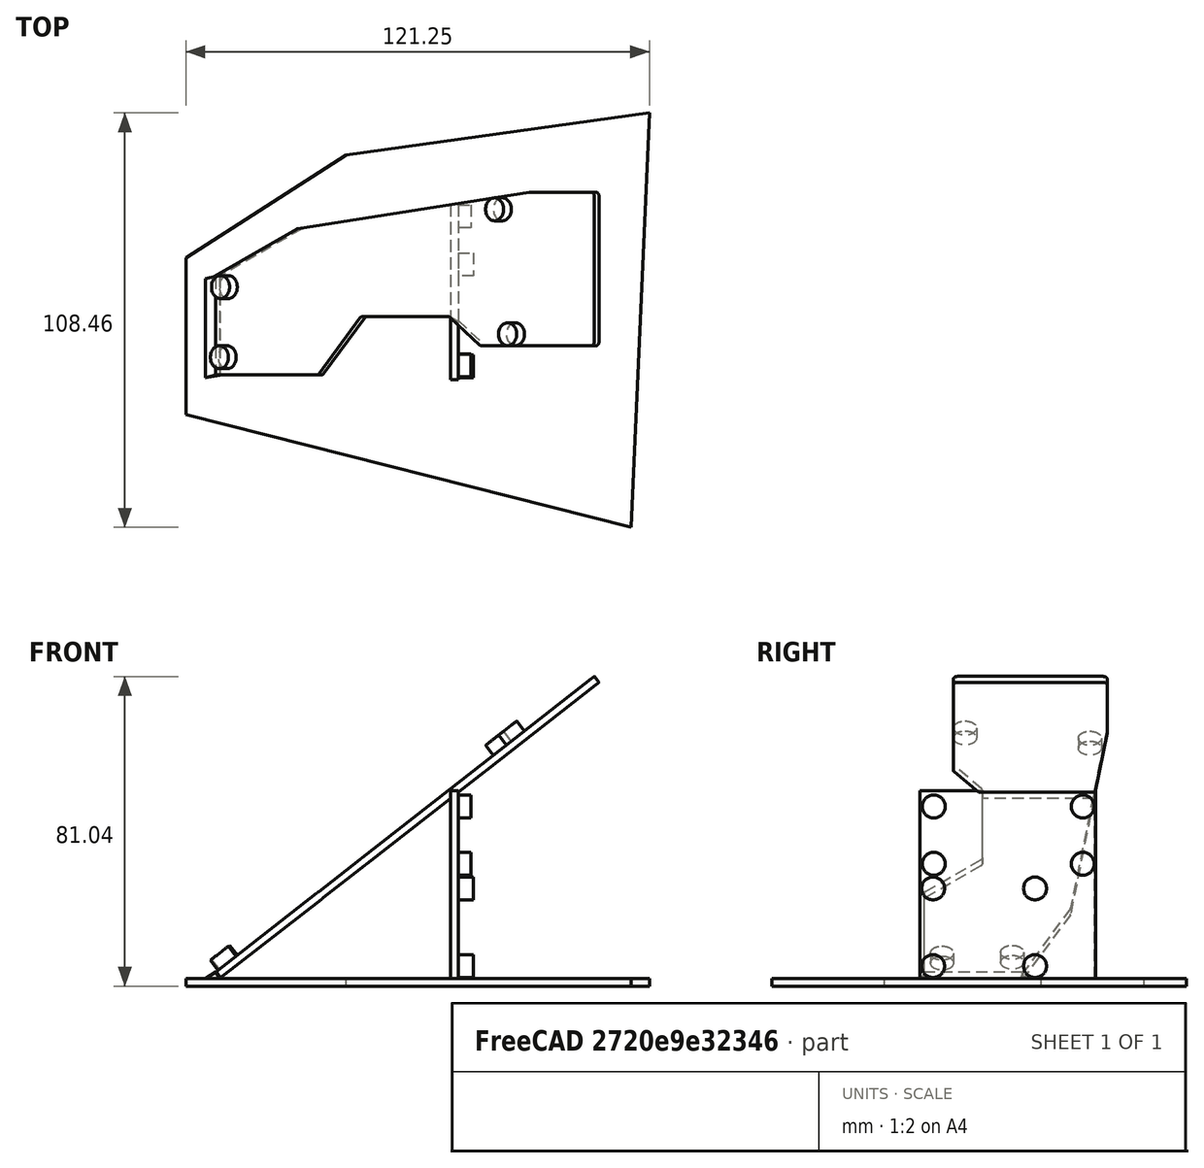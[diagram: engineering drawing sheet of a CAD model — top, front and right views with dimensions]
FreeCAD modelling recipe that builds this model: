
FCSTD DOCUMENT  (FreeCAD 1.0RUnknown)
Label: case-tent
License: All rights reserved
LicenseURL: https://en.wikipedia.org/wiki/All_rights_reserved
objects: Sketcher::SketchObject×9, PartDesign::Pad×7, App::Link×4, App::FeaturePython×4, PartDesign::Plane×2, PartDesign::Body×1, App::Part×1, Assembly::JointGroup×1, Assembly::AssemblyObject×1
note: 42 computed .brp shape members not serialized (recipe doc carries the construction recipe); baked Part::Feature solids carry a one-line shape summary decoded from their .brp
EXTERNAL_REF file=left.FCStd obj=Board_f9e4
EXTERNAL_REF file=thumb-cluster.FCStd obj=Board_58ce
EXTERNAL_REF file=thumbstick-breakout.FCStd obj=Board_bbd4

FEATURE [PartDesign::Plane] DatumPlane  label="tilt plane"
  AttachmentOffset = pos=(0,0,0) rot=(0,-1,0;0.663225rad)
  AttachmentSupport = -> [XY_Plane001]
  Length = 249.716
  MapMode = 5
  Placement = pos=(0,0,0) rot=(0,-1,0;0.663225rad)
  ResizeMode = 0
  Width = 139.285
FEATURE [Sketcher::SketchObject] PCB_Sketch_f9e006  label="left"
  ArcFitTolerance = 1e-06
  AttachmentOffset = pos=(0,3,4.4) rot=(0,0,1;0rad)
  AttachmentSupport = -> [DatumPlane]
  FullyConstrained = false
  MakeInternals = false
  MapMode = 5
  Placement = pos=(-2.70891,3,3.46725) rot=(0,-1,0;0.663225rad)
  sketch-geometry (22):
    g0: LineSegment StartX=48.9342 StartY=15.25 StartZ=0 EndX=77.5946 EndY=15.25 EndZ=0
    g1: LineSegment StartX=27.2503 StartY=38.2054 StartZ=0 EndX=0.008196 EndY=25.8215 EndZ=0
    g2: LineSegment StartX=126 StartY=8.65 StartZ=0 EndX=126 EndY=45.95 EndZ=0
    g3: LineSegment StartX=104.439 StartY=47.8424 StartZ=0 EndX=27.5489 EndY=38.289 EndZ=0
    g4: LineSegment StartX=34.5465 StartY=0.317255 StartZ=0 EndX=48.2035 EndY=14.9327 EndZ=0
    g5: LineSegment StartX=104.562 StartY=47.85 StartZ=0 EndX=125 EndY=47.85 EndZ=0
    g6: LineSegment StartX=125 StartY=7.65 StartZ=0 EndX=88.6266 EndY=7.65 EndZ=0
    g7: LineSegment StartX=0.008196 StartY=0 StartZ=0 EndX=33.8158 EndY=-1.6e-15 EndZ=0
    g8: LineSegment StartX=126 StartY=45.95 StartZ=0 EndX=126 EndY=46.85 EndZ=0
    g9: LineSegment StartX=78.291 StartY=14.9676 StartZ=0 EndX=88.0364 EndY=7.84274 EndZ=0
    g10: ArcOfCircle CenterX=27.666 CenterY=37.2959 CenterZ=0 NormalX=0 NormalY=0 NormalZ=-1 AngleXU=1.14211 Radius=1.00001 StartAngle=0 EndAngle=0.311303
    g11: ArcOfCircle CenterX=33.8158 CenterY=1.00002 CenterZ=0 NormalX=0 NormalY=0 NormalZ=-1 AngleXU=-2.39007 Radius=1.00002 StartAngle=0 EndAngle=0.81927
    g12: ArcOfCircle CenterX=48.9342 CenterY=14.25 CenterZ=0 NormalX=0 NormalY=0 NormalZ=-1 AngleXU=0.75152 Radius=1.00002 StartAngle=0 EndAngle=0.81927
    g13: ArcOfCircle CenterX=125 CenterY=46.85 CenterZ=0 NormalX=0 NormalY=0 NormalZ=-1 AngleXU=1.5708 Radius=0.999999 StartAngle=0 EndAngle=1.5708
    g14: ArcOfCircle CenterX=125 CenterY=8.65 CenterZ=0 NormalX=0 NormalY=0 NormalZ=-1 AngleXU=3.14159 Radius=0.999999 StartAngle=0 EndAngle=1.5708
    g15: ArcOfCircle CenterX=88.6266 CenterY=8.65 CenterZ=0 NormalX=0 NormalY=0 NormalZ=-1 AngleXU=-1.57079 Radius=1 StartAngle=0 EndAngle=0.631296
    g16: ArcOfCircle CenterX=104.562 CenterY=46.8498 CenterZ=0 NormalX=0 NormalY=0 NormalZ=-1 AngleXU=1.44719 Radius=1.00016 StartAngle=0 EndAngle=0.123594
    g17: ArcOfCircle CenterX=77.5946 CenterY=14.25 CenterZ=0 NormalX=0 NormalY=0 NormalZ=-1 AngleXU=1.57078 Radius=0.999961 StartAngle=0 EndAngle=0.770416
    g18: GeomPoint [constr] X=4.15 Y=4.65 Z=0
    g19: GeomPoint [constr] X=95.5 Y=43.35 Z=0
    g20: GeomPoint [constr] X=99.8333 Y=10.6833 Z=0
    g21: LineSegment StartX=0.008196 StartY=25.8215 StartZ=0 EndX=0.008196 EndY=0 EndZ=0
  constraints (20):
    c: Coincident(g1,g10)
    c: Coincident(g3,g10)
    c: Coincident(g7,g11)
    c: Coincident(g4,g11)
    c: Coincident(g4,g12)
    c: Coincident(g0,g12)
    c: Coincident(g0,g17)
    c: Coincident(g9,g17)
    c: Coincident(g9,g15)
    c: Coincident(g6,g15)
    c: Coincident(g3,g16)
    c: Coincident(g5,g16)
    c: Coincident(g6,g14)
    c: Coincident(g5,g13)
    c: Coincident(g2,g14)
    c: Coincident(g2,g8)
    c: Coincident(g8,g13)
    c: Coincident(g1,g21)
    c: Coincident(g21,g7)
    c: Vertical(g21)
FEATURE [PartDesign::Pad] Pad
  Direction = (-0.615661,0,0.788011)
  Length = 2
  Length2 = 10
  Placement = pos=(0,0,0) rot=(0,-1,0;0.663225rad)
  Profile = -> PCB_Sketch_f9e006
  ReferenceAxis = -> PCB_Sketch_f9e006 [N_Axis]
  Refine = true
  Reversed = true
  Suppressed = false
  Type = 0
FEATURE [PartDesign::Plane] DatumPlane001
  AttachmentOffset = pos=(0,0,2) rot=(0,0,1;0rad)
  AttachmentSupport = -> [XY_Plane001]
  Length = 193.247
  MapMode = 5
  Placement = pos=(0,0,2) rot=(0,0,1;0rad)
  ResizeMode = 0
  Width = 135.335
FEATURE [Sketcher::SketchObject] Sketch001
  ArcFitTolerance = 1e-06
  FullyConstrained = true
  MakeInternals = false
  MapMode = 5
  Placement = pos=(0.0069506,0,0.00434322) rot=(0.658342,-0.658342,-0.364925;2.44177rad)
  sketch-geometry (4):
    g0: LineSegment StartX=-28.8215 StartY=4.4 StartZ=0 EndX=-28.8215 EndY=2.4 EndZ=0
    g1: LineSegment StartX=-28.8215 StartY=2.4 StartZ=0 EndX=-3 EndY=2.4 EndZ=0
    g2: LineSegment StartX=-3 StartY=2.4 StartZ=0 EndX=-3 EndY=4.4 EndZ=0
    g3: LineSegment StartX=-3 StartY=4.4 StartZ=0 EndX=-28.8215 EndY=4.4 EndZ=0
  constraints (10):
    c: Coincident(g0,g1)
    c: Coincident(g1,g2)
    c: Coincident(g2,g3)
    c: Coincident(g3,g0)
    c: Vertical(g0)
    c: Vertical(g2)
    c: Horizontal(g1)
    c: Horizontal(g3)
    c: Coincident(g0,g-4)
    c: Coincident(g1,g-6)
FEATURE [PartDesign::Pad] Pad002
  BaseFeature = -> Pad
  Direction = (-0.85,-0.2,-0.53)
  Length = 10
  Length2 = 10
  Placement = pos=(0,0,0) rot=(0,-1,0;0.663225rad)
  Profile = -> Sketch001
  ReferenceAxis = -> Sketch001 [N_Axis]
  Refine = true
  Suppressed = false
  Type = 5
  UpToShape = -> [DatumPlane001]
  UseCustomVector = true
FEATURE [Sketcher::SketchObject] Sketch
  ArcFitTolerance = 1e-06
  AttachmentSupport = -> [XY_Plane001]
  FullyConstrained = false
  MakeInternals = false
  MapMode = 5
  sketch-geometry (5):
    g0: LineSegment StartX=-10.2101 StartY=33.6647 StartZ=0 EndX=-10.2101 EndY=-7.34119 EndZ=0
    g1: LineSegment StartX=-10.2101 StartY=-7.34119 StartZ=0 EndX=106.194 EndY=-36.883 EndZ=0
    g2: LineSegment StartX=106.194 StartY=-36.883 StartZ=0 EndX=111.044 EndY=71.5841 EndZ=0
    g3: LineSegment StartX=111.044 StartY=71.5841 StartZ=0 EndX=31.6776 EndY=60.561 EndZ=0
    g4: LineSegment StartX=31.6776 StartY=60.561 StartZ=0 EndX=-10.2101 EndY=33.6647 EndZ=0
  constraints (6):
    c: Vertical(g0)
    c: Coincident(g0,g1)
    c: Coincident(g1,g2)
    c: Coincident(g2,g3)
    c: Coincident(g3,g4)
    c: Coincident(g4,g0)
FEATURE [PartDesign::Pad] Pad003
  BaseFeature = -> Pad002
  Direction = (0,0,1)
  Length = 2
  Length2 = 10
  Placement = pos=(0,0,0) rot=(0,-1,0;0.663225rad)
  Profile = -> Sketch
  ReferenceAxis = -> Sketch [N_Axis]
  Refine = true
  Suppressed = false
  Type = 0
FEATURE [Sketcher::SketchObject] Sketch002
  ArcFitTolerance = 1e-06
  AttachmentSupport = -> [XY_Plane001]
  FullyConstrained = false
  MakeInternals = false
  MapMode = 5
  sketch-geometry (5):
    g0: LineSegment StartX=58.9852 StartY=17.9676 StartZ=0 EndX=58.9852 EndY=1.83853 EndZ=0
    g1: LineSegment StartX=58.9852 StartY=1.83853 StartZ=0 EndX=60.9852 EndY=1.83853 EndZ=0
    g2: LineSegment StartX=60.9852 StartY=1.83853 StartZ=0 EndX=60.9852 EndY=47.9089 EndZ=0
    g3: LineSegment StartX=60.9852 StartY=47.9089 StartZ=0 EndX=58.9852 EndY=47.5936 EndZ=0
    g4: LineSegment StartX=58.9852 StartY=47.5936 StartZ=0 EndX=58.9852 EndY=17.9676 EndZ=0
  constraints (13):
    c: Coincident(g-3,g0)
    c: Vertical(g0)
    c: Coincident(g0,g1)
    c: Horizontal(g1)
    c: Coincident(g1,g2)
    c: PointOnObject(g2,g-4)
    c: Vertical(g2)
    c: Coincident(g2,g3)
    c: PointOnObject(g3,g-4)
    c: Coincident(g3,g4)
    c: Coincident(g4,g0)
    c: Vertical(g4)
    c: DistanceX(g1,g1) = 2
FEATURE [PartDesign::Pad] Pad004
  BaseFeature = -> Pad003
  Direction = (0,0,1)
  Length = 51.1
  Length2 = 10
  Placement = pos=(0,0,0) rot=(0,-1,0;0.663225rad)
  Profile = -> Sketch002
  ReferenceAxis = -> Sketch002 [N_Axis]
  Refine = true
  Suppressed = false
  Type = 0
FEATURE [Sketcher::SketchObject] PCB_Sketch_58ce  label="thumb cluster"
  ArcFitTolerance = 1e-06
  AttachmentOffset = pos=(2.5,50,0) rot=(0,0,1;-1.5708rad)
  AttachmentSupport = -> [Pad004]
  FullyConstrained = false
  MakeInternals = false
  MapMode = 5
  Placement = pos=(60.9852,2.5,50) rot=(0,-1,0;4.71239rad)
  sketch-geometry (16):
    g0: LineSegment StartX=21 StartY=44 StartZ=0 EndX=21 EndY=1 EndZ=0
    g1: LineSegment StartX=20 StartY=1e-16 StartZ=0 EndX=1 EndY=0 EndZ=0
    g2: LineSegment StartX=1 StartY=45 StartZ=0 EndX=20 EndY=45 EndZ=0
    g3: LineSegment StartX=1e-16 StartY=1 StartZ=0 EndX=3.3e-15 EndY=44 EndZ=0
    g4: ArcOfCircle CenterX=20 CenterY=44 CenterZ=0 NormalX=0 NormalY=0 NormalZ=-1 AngleXU=1.5708 Radius=0.999999 StartAngle=0 EndAngle=1.5708
    g5: ArcOfCircle CenterX=0.999999 CenterY=0.999999 CenterZ=0 NormalX=0 NormalY=0 NormalZ=-1 AngleXU=-1.5708 Radius=0.999999 StartAngle=0 EndAngle=1.5708
    g6: ArcOfCircle CenterX=20 CenterY=0.999999 CenterZ=0 NormalX=0 NormalY=0 NormalZ=-1 AngleXU=3.14159 Radius=0.999999 StartAngle=0 EndAngle=1.5708
    g7: ArcOfCircle CenterX=0.999999 CenterY=44 CenterZ=0 NormalX=0 NormalY=0 NormalZ=-1 AngleXU=-7.47076e-07 Radius=0.999999 StartAngle=0 EndAngle=1.5708
    g8: GeomPoint [constr] X=3 Y=42 Z=0
    g9: GeomPoint [constr] X=18 Y=42 Z=0
    g10: GeomPoint [constr] X=18 Y=3 Z=0
    g11: GeomPoint [constr] X=3 Y=3 Z=0
    g12: Circle CenterX=3 CenterY=42 CenterZ=0 NormalX=0 NormalY=0 NormalZ=1 AngleXU=0 Radius=3
    g13: Circle CenterX=18 CenterY=42 CenterZ=0 NormalX=0 NormalY=0 NormalZ=1 AngleXU=0 Radius=3
    g14: Circle CenterX=18 CenterY=3 CenterZ=0 NormalX=0 NormalY=0 NormalZ=1 AngleXU=0 Radius=3
    g15: Circle CenterX=3 CenterY=3 CenterZ=0 NormalX=0 NormalY=0 NormalZ=1 AngleXU=0 Radius=3
  constraints (18):
    c: Coincident(g3,g5)
    c: Coincident(g3,g7)
    c: Coincident(g1,g5)
    c: Coincident(g2,g7)
    c: Coincident(g1,g6)
    c: Coincident(g2,g4)
    c: Coincident(g0,g6)
    c: Coincident(g0,g4)
    c: Diameter(g12) = 6
    c: Coincident(g12,g8)
    c: Diameter(g13) = 6
    c: Coincident(g13,g9)
    c: Tangent(g13,g0)
    c: Diameter(g14) = 6
    c: Coincident(g14,g10)
    c: Tangent(g14,g0)
    c: Diameter(g15) = 6
    c: Coincident(g15,g11)
FEATURE [Sketcher::SketchObject] PCB_Sketch_bbd4  label="thumbstick"
  ArcFitTolerance = 1e-06
  AttachmentOffset = pos=(40.5,2.7,0) rot=(0,0,1;1.5708rad)
  AttachmentSupport = -> [Pad004]
  FullyConstrained = false
  MakeInternals = false
  MapMode = 5
  Placement = pos=(60.9852,40.5,2.7) rot=(0.707107,0,0.707107;3.14159rad)
  sketch-geometry (12):
    g0: LineSegment StartX=0 StartY=37.72 StartZ=0 EndX=0 EndY=0 EndZ=0
    g1: LineSegment StartX=25.4 StartY=37.72 StartZ=0 EndX=0 EndY=37.72 EndZ=0
    g2: LineSegment StartX=0 StartY=0 StartZ=0 EndX=25.4 EndY=0 EndZ=0
    g3: LineSegment StartX=25.4 StartY=0 StartZ=0 EndX=25.4 EndY=37.72 EndZ=0
    g4: GeomPoint [constr] X=2.54 Y=35.18 Z=0
    g5: GeomPoint [constr] X=22.86 Y=35.18 Z=0
    g6: GeomPoint [constr] X=22.86 Y=8.51 Z=0
    g7: GeomPoint [constr] X=2.54 Y=8.51 Z=0
    g8: Circle CenterX=22.86 CenterY=35.18 CenterZ=0 NormalX=0 NormalY=0 NormalZ=1 AngleXU=0 Radius=3
    g9: Circle CenterX=2.54 CenterY=35.18 CenterZ=0 NormalX=0 NormalY=0 NormalZ=1 AngleXU=0 Radius=3
    g10: Circle CenterX=2.54 CenterY=8.51 CenterZ=0 NormalX=0 NormalY=0 NormalZ=1 AngleXU=0 Radius=3
    g11: Circle CenterX=22.86 CenterY=8.51 CenterZ=0 NormalX=0 NormalY=0 NormalZ=1 AngleXU=0 Radius=3
  constraints (12):
    c: Coincident(g0,g2)
    c: Coincident(g0,g1)
    c: Coincident(g2,g3)
    c: Coincident(g1,g3)
    c: Diameter(g8) = 6
    c: Coincident(g8,g5)
    c: Diameter(g9) = 6
    c: Coincident(g9,g4)
    c: Diameter(g10) = 6
    c: Coincident(g10,g7)
    c: Diameter(g11) = 6
    c: Coincident(g11,g6)
FEATURE [Sketcher::SketchObject] Sketch003
  ArcFitTolerance = 1e-06
  AttachmentSupport = -> [Pad004]
  FullyConstrained = false
  MakeInternals = false
  MapMode = 5
  Placement = pos=(-2.70891,0,3.46725) rot=(0,-1,0;0.663225rad)
  sketch-geometry (4):
    g0: Circle CenterX=4.49466 CenterY=26.0177 CenterZ=0 NormalX=0 NormalY=0 NormalZ=1 AngleXU=0 Radius=3
    g1: Circle CenterX=4.15 CenterY=7.65 CenterZ=0 NormalX=0 NormalY=0 NormalZ=1 AngleXU=0 Radius=3
    g2: Circle CenterX=95.5 CenterY=46.35 CenterZ=0 NormalX=0 NormalY=0 NormalZ=1 AngleXU=0 Radius=3
    g3: Circle CenterX=99.8333 CenterY=13.6833 CenterZ=0 NormalX=0 NormalY=0 NormalZ=1 AngleXU=0 Radius=3
FEATURE [PartDesign::Pad] Pad005
  BaseFeature = -> Pad004
  Direction = (-0.615661,0,0.788011)
  Length = 3.3
  Length2 = 10
  Placement = pos=(0,0,0) rot=(0,-1,0;0.663225rad)
  Profile = -> Sketch003
  ReferenceAxis = -> Sketch003 [N_Axis]
  Refine = true
  Suppressed = false
  Type = 0
FEATURE [Sketcher::SketchObject] Sketch004
  ArcFitTolerance = 1e-06
  AttachmentSupport = -> [Pad005]
  ExternalGeometry = -> [PCB_Sketch_58ce]
  FullyConstrained = true
  MakeInternals = false
  MapMode = 5
  Placement = pos=(60.9852,0,4.74e-14) rot=(0.57735,0.57735,0.57735;2.0944rad)
  sketch-geometry (4):
    g0: Circle CenterX=5.5 CenterY=47 CenterZ=0 NormalX=0 NormalY=0 NormalZ=1 AngleXU=0 Radius=3
    g1: Circle CenterX=44.5 CenterY=47 CenterZ=0 NormalX=0 NormalY=0 NormalZ=1 AngleXU=0 Radius=3
    g2: Circle CenterX=44.5 CenterY=32 CenterZ=0 NormalX=0 NormalY=0 NormalZ=1 AngleXU=0 Radius=3
    g3: Circle CenterX=5.5 CenterY=32 CenterZ=0 NormalX=0 NormalY=0 NormalZ=1 AngleXU=0 Radius=3
  constraints (8):
    c: Coincident(g0,g-3)
    c: Equal(g0,g-3)
    c: Coincident(g1,g-4)
    c: Equal(g1,g-4)
    c: Coincident(g2,g-5)
    c: Equal(g2,g-5)
    c: Coincident(g3,g-6)
    c: Equal(g3,g-6)
FEATURE [PartDesign::Pad] Pad006
  BaseFeature = -> Pad005
  Direction = (1,0,0)
  Length = 3.3
  Length2 = 10
  Placement = pos=(0,0,0) rot=(0,-1,0;0.663225rad)
  Profile = -> Sketch004
  ReferenceAxis = -> Sketch004 [N_Axis]
  Refine = true
  Suppressed = false
  Type = 0
FEATURE [Sketcher::SketchObject] Sketch005
  ArcFitTolerance = 1e-06
  AttachmentSupport = -> [Pad006]
  ExternalGeometry = -> [PCB_Sketch_bbd4]
  FullyConstrained = true
  MakeInternals = false
  MapMode = 5
  Placement = pos=(60.9852,0,7.45e-14) rot=(0.57735,0.57735,0.57735;2.0944rad)
  sketch-geometry (4):
    g0: Circle CenterX=5.32 CenterY=25.56 CenterZ=0 NormalX=0 NormalY=0 NormalZ=1 AngleXU=0 Radius=3
    g1: Circle CenterX=31.99 CenterY=25.56 CenterZ=0 NormalX=0 NormalY=0 NormalZ=1 AngleXU=0 Radius=3
    g2: Circle CenterX=31.99 CenterY=5.24 CenterZ=0 NormalX=0 NormalY=0 NormalZ=1 AngleXU=0 Radius=3
    g3: Circle CenterX=5.32 CenterY=5.24 CenterZ=0 NormalX=0 NormalY=0 NormalZ=1 AngleXU=0 Radius=3
  constraints (8):
    c: Coincident(g0,g-3)
    c: Equal(g0,g-3)
    c: Coincident(g1,g-5)
    c: Equal(g1,g-5)
    c: Coincident(g2,g-6)
    c: Equal(g2,g-6)
    c: Coincident(g3,g-4)
    c: Equal(g3,g-4)
FEATURE [PartDesign::Pad] Pad007
  BaseFeature = -> Pad006
  Direction = (1,0,1.3e-15)
  Length = 4
  Length2 = 10
  Placement = pos=(0,0,0) rot=(0,-1,0;0.663225rad)
  Profile = -> Sketch005
  ReferenceAxis = -> Sketch005 [N_Axis]
  Refine = true
  Suppressed = false
  Type = 0
FEATURE [PartDesign::Body] Body
  AllowCompound = false
  Group = -> [DatumPlane,PCB_Sketch_f9e006,Pad,PCB_Sketch_58ce,DatumPlane001,PCB_Sketch_bbd4,Sketch001,Pad002,Sketch,Pad003,Sketch002,Pad004,Sketch003,Pad005,Sketch004,Pad006,Sketch005,Pad007]
  Origin = -> Origin001
  Tip = -> Pad007
FEATURE [App::Part] Part
  Group = -> [Body]
  Origin = -> Origin
FEATURE [App::Link] Part001
  LinkedObject = -> Part
FEATURE [App::FeaturePython] GroundedJoint  # Assembly grounded joint (typed FeaturePython)
  ObjectToGround = -> Part001
FEATURE [App::Link] left  label="left001"
  LinkPlacement = pos=(-5.72565,3,7.3285) rot=(0,-1,0;0.663225rad)
  LinkedObject = -> <external left.FCStd>#Board_f9e4
  Placement = pos=(-5.72565,3,7.3285) rot=(0,-1,0;0.663225rad)
FEATURE [App::Link] thumb_cluster  label="thumb-cluster"
  LinkPlacement = pos=(65.8852,2.5,50) rot=(0,1,0;1.5708rad)
  LinkedObject = -> <external thumb-cluster.FCStd>#Board_58ce
  Placement = pos=(65.8852,2.5,50) rot=(0,1,0;1.5708rad)
FEATURE [App::Link] thumbstick_breakout  label="thumbstick-breakout"
  LinkPlacement = pos=(66.5852,40.5,2.7) rot=(0.707107,0,0.707107;3.14159rad)
  LinkedObject = -> <external thumbstick-breakout.FCStd>#Board_bbd4
  Placement = pos=(66.5852,40.5,2.7) rot=(0.707107,0,0.707107;3.14159rad)
FEATURE [App::FeaturePython] Joint  label="Fixed"  # Assembly joint (typed FeaturePython)
  Activated = true
  AngleMax = 0
  AngleMin = 0
  Detach1 = false
  Detach2 = false
  Distance = 0
  Distance2 = 0
  EnableAngleMax = false
  EnableAngleMin = false
  EnableLengthMax = false
  EnableLengthMin = false
  JointType = 0 (Fixed)
  LengthMax = 0
  LengthMin = 0
  Placement1 = pos=(115,-64.5,-1.6) rot=(0,0,1;0rad)
  Placement2 = pos=(70.5144,46.35,64.8634) rot=(0,-1,0;0.663225rad)
  Reference1 = -> Assembly [left.Board_Geoms_f9e4.Pcb_f9e4.Edge327,left.Board_Geoms_f9e4.Pcb_f9e4.Edge327]
  Reference2 = -> Assembly [Part001.Body.Edge87,Part001.Body.Edge87]
FEATURE [App::FeaturePython] Joint001  label="Fixed001"  # Assembly joint (typed FeaturePython)
  Activated = true
  AngleMax = 0
  AngleMin = 0
  Detach1 = false
  Detach2 = false
  Distance = 0
  Distance2 = 0
  EnableAngleMax = false
  EnableAngleMin = false
  EnableLengthMax = false
  EnableLengthMin = false
  JointType = 0 (Fixed)
  LengthMax = 0
  LengthMin = 0
  Offset2 = pos=(0,0,0) rot=(0,0,1;1.5708rad)
  Placement1 = pos=(64.2852,44.5,47) rot=(0.57735,0.57735,0.57735;2.0944rad)
  Placement2 = pos=(22.5,-27,-1.6) rot=(0,0,1;1.5708rad)
  Reference1 = -> Assembly [Part001.Body.Edge139,Part001.Body.Edge139]
  Reference2 = -> Assembly [thumb_cluster.Board_Geoms_58ce.Pcb_58ce.Edge135,thumb_cluster.Board_Geoms_58ce.Pcb_58ce.Edge135]
FEATURE [App::FeaturePython] Joint002  label="Fixed002"  # Assembly joint (typed FeaturePython)
  Activated = true
  AngleMax = 0
  AngleMin = 0
  Detach1 = false
  Detach2 = false
  Distance = 0
  Distance2 = 0
  EnableAngleMax = false
  EnableAngleMin = false
  EnableLengthMax = false
  EnableLengthMin = false
  JointType = 0 (Fixed)
  LengthMax = 0
  LengthMin = 0
  Offset2 = pos=(0,0,0) rot=(0,0,-1;1.5708rad)
  Placement1 = pos=(64.9852,5.32,5.24) rot=(0.57735,0.57735,0.57735;2.0944rad)
  Placement2 = pos=(139.84,-88.57,-1.6) rot=(0,0,-1;1.5708rad)
  Reference1 = -> Assembly [Part001.Body.Edge145,Part001.Body.Edge145]
  Reference2 = -> Assembly [thumbstick_breakout.Board_Geoms_bbd4.Pcb_bbd4.Edge63,thumbstick_breakout.Board_Geoms_bbd4.Pcb_bbd4.Edge63]
FEATURE [Assembly::JointGroup] Joints
  Group = -> [GroundedJoint,Joint,Joint001,Joint002]
FEATURE [Assembly::AssemblyObject] Assembly
  Group = -> [Joints,Part001,GroundedJoint,left,thumb_cluster,thumbstick_breakout,Joint,Joint001,Joint002]
  Origin = -> Origin002
  Type = Assembly

RESOLVED EXTERNAL PARTS (link-assembly join: the EXTERNAL_REF files above that resolve inside this repo's crawl, each included once):
---- part left.FCStd = doc fcstd_3019e020500d (78541 chars; too large to inline — full recipe in that document) ----
---- part thumb-cluster.FCStd = doc fcstd_5160b2ce58e3 ----
FCSTD DOCUMENT  (FreeCAD 1.0RUnknown)
Label: thumb-cluster
License: All rights reserved
LicenseURL: https://en.wikipedia.org/wiki/All_rights_reserved
objects: Part::Feature×14, Sketcher::SketchObject×10, App::Link×10, App::Part×6, PartDesign::Pocket×4, PartDesign::Pad×3, PartDesign::Chamfer×3, PartDesign::Thickness×2, PartDesign::Body×2, PartDesign::SubShapeBinder×2, PartDesign::CoordinateSystem×1, PartDesign::ShapeBinder×1
note: 76 computed .brp shape members not serialized (recipe doc carries the construction recipe); baked Part::Feature solids carry a one-line shape summary decoded from their .brp

FEATURE [PartDesign::CoordinateSystem] Local_CS_58ce
  AttacherType = Attacher::AttachEngine3D
  MapMode = 2
FEATURE [Part::Feature] Pcb_58ce
  Placement = pos=(-19.5,69,0) rot=(0,0,1;0rad)
  shape: bbox 21 x 45 x 1.6 mm, 50 faces (baked)
FEATURE [Sketcher::SketchObject] PCB_Sketch_58ce
  ArcFitTolerance = 1e-06
  FullyConstrained = false
  MakeInternals = false
  sketch-geometry (8):
    g0: LineSegment StartX=21 StartY=44 StartZ=0 EndX=21 EndY=1 EndZ=0
    g1: LineSegment StartX=20 StartY=1e-16 StartZ=0 EndX=1 EndY=0 EndZ=0
    g2: LineSegment StartX=1 StartY=45 StartZ=0 EndX=20 EndY=45 EndZ=0
    g3: LineSegment StartX=1e-16 StartY=1 StartZ=0 EndX=3.3e-15 EndY=44 EndZ=0
    g4: ArcOfCircle CenterX=20 CenterY=44 CenterZ=0 NormalX=0 NormalY=0 NormalZ=-1 AngleXU=1.5708 Radius=0.999999 StartAngle=0 EndAngle=1.5708
    g5: ArcOfCircle CenterX=0.999999 CenterY=0.999999 CenterZ=0 NormalX=0 NormalY=0 NormalZ=-1 AngleXU=-1.5708 Radius=0.999999 StartAngle=0 EndAngle=1.5708
    g6: ArcOfCircle CenterX=20 CenterY=0.999999 CenterZ=0 NormalX=0 NormalY=0 NormalZ=-1 AngleXU=3.14159 Radius=0.999999 StartAngle=0 EndAngle=1.5708
    g7: ArcOfCircle CenterX=0.999999 CenterY=44 CenterZ=0 NormalX=0 NormalY=0 NormalZ=-1 AngleXU=-7.47076e-07 Radius=0.999999 StartAngle=0 EndAngle=1.5708
  constraints (8):
    c: Coincident(g3,g5)
    c: Coincident(g3,g7)
    c: Coincident(g1,g5)
    c: Coincident(g2,g7)
    c: Coincident(g1,g6)
    c: Coincident(g2,g4)
    c: Coincident(g0,g6)
    c: Coincident(g0,g4)
FEATURE [App::Part] Board_Geoms_58ce
  Group = -> [Pcb_58ce,PCB_Sketch_58ce]
  Origin = -> Origin
FEATURE [Part::Feature] Shape  label="D24_D_SOD_123_0f779e6ff9e7"
  Placement = pos=(3.66673,13.8333,0) rot=(0,0,-1;0.785398rad)
  shape: bbox 3.147 x 3.147 x 1.25 mm, 67 faces (baked)
FEATURE [Part::Feature] Shape001  label="J4_SOLID_42e36dcc9d63"
  Placement = pos=(10.9645,42.4,0) rot=(0,0.707107,0.707107;3.14159rad)
  shape: bbox 5.501 x 4.001 x 0.9009 mm, 979 faces (baked)
FEATURE [App::Link] D24_D_SOD_123_0f779e6ff9e7_ln_  label="D23_D_SOD_123_3fd67df90355"
  LinkPlacement = pos=(5.66673,15.8333,0) rot=(0,0,-1;0.785398rad)
  LinkedObject = -> Shape
  Placement = pos=(5.66673,15.8333,0) rot=(0,0,-1;0.785398rad)
FEATURE [App::Link] D24_D_SOD_123_0f779e6ff9e7_ln_001  label="D30_D_SOD_123_61e72e2af53f"
  LinkPlacement = pos=(19.75,16.55,0) rot=(0,0,-1;1.5708rad)
  LinkedObject = -> Shape
  Placement = pos=(19.75,16.55,0) rot=(0,0,-1;1.5708rad)
FEATURE [App::Link] D24_D_SOD_123_0f779e6ff9e7_ln_002  label="D27_D_SOD_123_7b2efe9b5669"
  LinkPlacement = pos=(17.6667,24.3333,0) rot=(0,0,1;2.35619rad)
  LinkedObject = -> Shape
  Placement = pos=(17.6667,24.3333,0) rot=(0,0,1;2.35619rad)
FEATURE [App::Link] D24_D_SOD_123_0f779e6ff9e7_ln_003  label="D22_D_SOD_123_057a97edfa83"
  LinkPlacement = pos=(7.66673,17.8333,0) rot=(0,0,-1;0.785398rad)
  LinkedObject = -> Shape
  Placement = pos=(7.66673,17.8333,0) rot=(0,0,-1;0.785398rad)
FEATURE [App::Link] D24_D_SOD_123_0f779e6ff9e7_ln_004  label="D29_D_SOD_123_cdf521000048"
  LinkPlacement = pos=(16.5,16.55,0) rot=(0,0,-1;1.5708rad)
  LinkedObject = -> Shape
  Placement = pos=(16.5,16.55,0) rot=(0,0,-1;1.5708rad)
FEATURE [App::Link] D24_D_SOD_123_0f779e6ff9e7_ln_005  label="D28_D_SOD_123_d5d7d507dfc1"
  LinkPlacement = pos=(15.6667,22.3333,0) rot=(0,0,1;2.35619rad)
  LinkedObject = -> Shape
  Placement = pos=(15.6667,22.3333,0) rot=(0,0,1;2.35619rad)
FEATURE [App::Link] D24_D_SOD_123_0f779e6ff9e7_ln_006  label="D20_D_SOD_123_675b5f77a9ad"
  LinkPlacement = pos=(5.16673,33.8333,0) rot=(0,0,-1;0.785398rad)
  LinkedObject = -> Shape
  Placement = pos=(5.16673,33.8333,0) rot=(0,0,-1;0.785398rad)
FEATURE [Part::Feature] Part__Feature  label="SKRHAD"
  shape: bbox 7.483 x 7.5 x 5.5 mm, 242 faces (baked)
FEATURE [Part::Feature] Part__Feature001  label="Pins"
  shape: bbox 1.15 x 0.8 x 0.1 mm, 6 faces (baked)
FEATURE [Part::Feature] Part__Feature002  label="Pins001"
  shape: bbox 1.15 x 0.8 x 0.1 mm, 6 faces (baked)
FEATURE [Part::Feature] Part__Feature003  label="Pins002"
  shape: bbox 1.15 x 0.8 x 0.1 mm, 6 faces (baked)
FEATURE [Part::Feature] Part__Feature004  label="Pins003"
  shape: bbox 1.15 x 0.8 x 0.1 mm, 6 faces (baked)
FEATURE [Part::Feature] Part__Feature005  label="Pins004"
  shape: bbox 1.15 x 0.8 x 0.1 mm, 6 faces (baked)
FEATURE [Part::Feature] Part__Feature006  label="Pins005"
  shape: bbox 1.15 x 0.8 x 0.1 mm, 6 faces (baked)
FEATURE [Part::Feature] Part__Feature007  label="Pins006"
  shape: bbox 1.64 x 1.44 x 0.1 mm, 6 faces (baked)
FEATURE [Part::Feature] Part__Feature008  label="Pins007"
  shape: bbox 1.64 x 1.44 x 0.1 mm, 6 faces (baked)
FEATURE [Part::Feature] Part__Feature009  label="Lugs"
  shape: bbox 0.55 x 0.55 x 1.8 mm, 3 faces (baked)
FEATURE [Part::Feature] Part__Feature010  label="Lugs001"
  shape: bbox 0.85 x 0.85 x 1.8 mm, 3 faces (baked)
FEATURE [App::Part] SKRHADE  label="S6_SKRHADE_66ce9957abdd"
  Group = -> [Part__Feature,Part__Feature001,Part__Feature002,Part__Feature003,Part__Feature004,Part__Feature005,Part__Feature006,Part__Feature007,Part__Feature008,Part__Feature009,Part__Feature010]
  Origin = -> Origin008
  Placement = pos=(10.9645,9.96447,0) rot=(0,0,-1;0.785398rad)
FEATURE [App::Link] D24_D_SOD_123_0f779e6ff9e7_ln_007  label="D21_D_SOD_123_014bcfdeeddd"
  LinkPlacement = pos=(3.16673,31.8333,0) rot=(0,0,-1;0.785398rad)
  LinkedObject = -> Shape
  Placement = pos=(3.16673,31.8333,0) rot=(0,0,-1;0.785398rad)
FEATURE [App::Link] D24_D_SOD_123_0f779e6ff9e7_ln_008  label="D19_D_SOD_123_2a26592c9c0c"
  LinkPlacement = pos=(7.16673,35.8333,0) rot=(0,0,-1;0.785398rad)
  LinkedObject = -> Shape
  Placement = pos=(7.16673,35.8333,0) rot=(0,0,-1;0.785398rad)
FEATURE [App::Link] S6_SKRHADE_66ce9957abdd_ln_  label="S5_SKRHADE_e4e283c67a98"
  LinkPlacement = pos=(10.9645,28.5203,0) rot=(0,0,-1;0.785398rad)
  LinkedObject = -> SKRHADE
  Placement = pos=(10.9645,28.5203,0) rot=(0,0,-1;0.785398rad)
FEATURE [App::Part] Top_58ce
  Group = -> [Shape,Shape001,D24_D_SOD_123_0f779e6ff9e7_ln_,D24_D_SOD_123_0f779e6ff9e7_ln_001,D24_D_SOD_123_0f779e6ff9e7_ln_002,D24_D_SOD_123_0f779e6ff9e7_ln_003,D24_D_SOD_123_0f779e6ff9e7_ln_004,D24_D_SOD_123_0f779e6ff9e7_ln_005,D24_D_SOD_123_0f779e6ff9e7_ln_006,SKRHADE,D24_D_SOD_123_0f779e6ff9e7_ln_007,D24_D_SOD_123_0f779e6ff9e7_ln_008,S6_SKRHADE_66ce9957abdd_ln_]
  Origin = -> Origin003
FEATURE [App::Part] Step_Models_58ce
  Group = -> [Top_58ce]
  Origin = -> Origin002
FEATURE [Sketcher::SketchObject] Sketch  label="2.2"
  ArcFitTolerance = 1e-06
  FullyConstrained = false
  MakeInternals = false
  Placement = pos=(0,0,0) rot=(0,0,1;3.14159rad)
  sketch-geometry (8):
    g0: LineSegment StartX=-23.2 StartY=-44 StartZ=0 EndX=-23.2 EndY=-0.999999 EndZ=0
    g1: ArcOfCircle CenterX=-20 CenterY=-0.999999 CenterZ=0 NormalX=0 NormalY=0 NormalZ=1 AngleXU=-3.14159 Radius=3.2 StartAngle=4.71239 EndAngle=6.28318
    g2: LineSegment StartX=-20 StartY=2.2 StartZ=0 EndX=-0.999999 EndY=2.2 EndZ=0
    g3: ArcOfCircle CenterX=-0.999999 CenterY=-0.999999 CenterZ=0 NormalX=0 NormalY=0 NormalZ=1 AngleXU=1.5708 Radius=3.2 StartAngle=4.71239 EndAngle=6.28318
    g4: LineSegment StartX=2.2 StartY=-0.999999 StartZ=0 EndX=2.2 EndY=-44 EndZ=0
    g5: ArcOfCircle CenterX=-0.999999 CenterY=-44 CenterZ=0 NormalX=0 NormalY=0 NormalZ=1 AngleXU=7.47076e-07 Radius=3.2 StartAngle=4.71239 EndAngle=6.28318
    g6: LineSegment StartX=-0.999999 StartY=-47.2 StartZ=0 EndX=-20 EndY=-47.2 EndZ=0
    g7: ArcOfCircle CenterX=-20 CenterY=-44 CenterZ=0 NormalX=0 NormalY=0 NormalZ=1 AngleXU=-1.5708 Radius=3.2 StartAngle=4.71239 EndAngle=6.28318
  constraints (12):
    c: Vertical(g0)
    c: Coincident(g0,g1)
    c: Coincident(g1,g2)
    c: Horizontal(g2)
    c: Coincident(g2,g3)
    c: Coincident(g3,g4)
    c: Vertical(g4)
    c: Coincident(g4,g5)
    c: Coincident(g5,g6)
    c: Horizontal(g6)
    c: Coincident(g6,g7)
    c: Coincident(g7,g0)
FEATURE [Sketcher::SketchObject] Sketch025  label="2.003"
  ArcFitTolerance = 1e-06
  FullyConstrained = false
  MakeInternals = false
  Placement = pos=(0,0,0) rot=(0,0,1;3.14159rad)
  sketch-geometry (8):
    g0: LineSegment StartX=-23.4 StartY=-44 StartZ=0 EndX=-23.4 EndY=-0.999999 EndZ=0
    g1: ArcOfCircle CenterX=-20 CenterY=-0.999999 CenterZ=0 NormalX=0 NormalY=0 NormalZ=1 AngleXU=0 Radius=3.4 StartAngle=1.5708 EndAngle=3.14159
    g2: LineSegment StartX=-20 StartY=2.4 StartZ=0 EndX=-0.999999 EndY=2.4 EndZ=0
    g3: ArcOfCircle CenterX=-0.999999 CenterY=-0.999999 CenterZ=0 NormalX=0 NormalY=0 NormalZ=1 AngleXU=0 Radius=3.4 StartAngle=6.28318 EndAngle=7.85398
    g4: LineSegment StartX=2.4 StartY=-1 StartZ=0 EndX=2.4 EndY=-44 EndZ=0
    g5: ArcOfCircle CenterX=-0.999999 CenterY=-44 CenterZ=0 NormalX=0 NormalY=0 NormalZ=1 AngleXU=0 Radius=3.4 StartAngle=4.71239 EndAngle=6.28318
    g6: LineSegment StartX=-0.999999 StartY=-47.4 StartZ=0 EndX=-20 EndY=-47.4 EndZ=0
    g7: ArcOfCircle CenterX=-20 CenterY=-44 CenterZ=0 NormalX=0 NormalY=0 NormalZ=1 AngleXU=0 Radius=3.4 StartAngle=3.14159 EndAngle=4.71239
  constraints (12):
    c: Vertical(g0)
    c: Coincident(g0,g1)
    c: Coincident(g1,g2)
    c: Horizontal(g2)
    c: Coincident(g2,g3)
    c: Coincident(g3,g4)
    c: Vertical(g4)
    c: Coincident(g4,g5)
    c: Coincident(g5,g6)
    c: Horizontal(g6)
    c: Coincident(g6,g7)
    c: Coincident(g7,g0)
FEATURE [PartDesign::Pad] Pad
  Direction = (0,0,1)
  Length = 3.2
  Length2 = 10
  Placement = pos=(0,0,0) rot=(0,0,1;3.14159rad)
  Profile = -> Sketch025
  ReferenceAxis = -> Sketch025 [N_Axis]
  Refine = true
  Suppressed = false
  Type = 0
FEATURE [PartDesign::Thickness] Thickness
  Base = -> Pad [Face10]
  BaseFeature = -> Pad
  Intersection = false
  Join = 0
  Mode = 0
  Refine = true
  Reversed = true
  SupportTransform = false
  Suppressed = false
  Value = 2
FEATURE [PartDesign::ShapeBinder] ShapeBinder
  Support = -> [Pcb_58ce]
  TraceSupport = false
FEATURE [Sketcher::SketchObject] Sketch026
  ArcFitTolerance = 1e-06
  AttachmentSupport = -> [Thickness]
  ExternalGeometry = -> [ShapeBinder]
  FullyConstrained = true
  MakeInternals = false
  MapMode = 5
  Placement = pos=(0,0,0) rot=(1,0,0;3.14159rad)
  sketch-geometry (4):
    g0: Circle CenterX=3 CenterY=-3 CenterZ=0 NormalX=0 NormalY=0 NormalZ=1 AngleXU=0 Radius=1.25
    g1: Circle CenterX=18 CenterY=-3 CenterZ=0 NormalX=0 NormalY=0 NormalZ=1 AngleXU=0 Radius=1.25
    g2: Circle CenterX=18 CenterY=-42 CenterZ=0 NormalX=0 NormalY=0 NormalZ=1 AngleXU=0 Radius=1.25
    g3: Circle CenterX=3 CenterY=-42 CenterZ=0 NormalX=0 NormalY=0 NormalZ=1 AngleXU=0 Radius=1.25
  constraints (8):
    c: Coincident(g0,g-3)
    c: Coincident(g1,g-4)
    c: Coincident(g2,g-5)
    c: Diameter(g2) = 2.5
    c: Equal(g0,g1)
    c: Equal(g1,g2)
    c: Coincident(g3,g-6)
    c: Equal(g2,g3)
FEATURE [PartDesign::Pocket] Pocket010
  BaseFeature = -> Thickness
  Direction = (0,0,1)
  Length = 5
  Length2 = 5
  Profile = -> Sketch026
  ReferenceAxis = -> Sketch026 [N_Axis]
  Refine = true
  Suppressed = false
  Type = 1
FEATURE [PartDesign::Chamfer] Chamfer001
  Angle = 60
  Base = -> Pocket010 [Edge18,Edge19,Edge16,Edge17]
  BaseFeature = -> Pocket010
  ChamferType = 2
  FlipDirection = false
  Refine = true
  Size = 0.8
  Size2 = 1
  SupportTransform = false
  Suppressed = false
  UseAllEdges = false
FEATURE [PartDesign::Body] Body010  label="base"
  AllowCompound = false
  Group = -> [Sketch025,Pad,Thickness,ShapeBinder,Sketch026,Pocket010,Chamfer001]
  Origin = -> Origin022
  Placement = pos=(0,0,-3.6) rot=(0,0,1;0rad)
  Tip = -> Chamfer001
FEATURE [Sketcher::SketchObject] Sketch027  label="2.004"
  ArcFitTolerance = 1e-06
  FullyConstrained = false
  MakeInternals = false
  Placement = pos=(0,0,0) rot=(0,0,1;3.14159rad)
  sketch-geometry (8):
    g0: LineSegment StartX=-23.4 StartY=-44 StartZ=0 EndX=-23.4 EndY=-1 EndZ=0
    g1: ArcOfCircle CenterX=-20 CenterY=-0.999999 CenterZ=0 NormalX=0 NormalY=0 NormalZ=1 AngleXU=0 Radius=3.4 StartAngle=1.5708 EndAngle=3.14159
    g2: LineSegment StartX=-20 StartY=2.4 StartZ=0 EndX=-1 EndY=2.4 EndZ=0
    g3: ArcOfCircle CenterX=-0.999999 CenterY=-0.999999 CenterZ=0 NormalX=0 NormalY=0 NormalZ=1 AngleXU=0 Radius=3.4 StartAngle=6.28318 EndAngle=7.85398
    g4: LineSegment StartX=2.4 StartY=-1 StartZ=0 EndX=2.4 EndY=-44 EndZ=0
    g5: ArcOfCircle CenterX=-0.999999 CenterY=-44 CenterZ=0 NormalX=0 NormalY=0 NormalZ=1 AngleXU=0 Radius=3.4 StartAngle=4.71239 EndAngle=6.28319
    g6: LineSegment StartX=-0.999999 StartY=-47.4 StartZ=0 EndX=-20 EndY=-47.4 EndZ=0
    g7: ArcOfCircle CenterX=-20 CenterY=-44 CenterZ=0 NormalX=0 NormalY=0 NormalZ=1 AngleXU=0 Radius=3.4 StartAngle=3.14159 EndAngle=4.71239
  constraints (12):
    c: Vertical(g0)
    c: Coincident(g0,g1)
    c: Coincident(g1,g2)
    c: Horizontal(g2)
    c: Coincident(g2,g3)
    c: Coincident(g3,g4)
    c: Vertical(g4)
    c: Coincident(g4,g5)
    c: Coincident(g5,g6)
    c: Horizontal(g6)
    c: Coincident(g6,g7)
    c: Coincident(g7,g0)
FEATURE [PartDesign::Pad] Pad014
  Direction = (0,0,1)
  Length = 5
  Length2 = 10
  Placement = pos=(0,0,0) rot=(0,0,1;3.14159rad)
  Profile = -> Sketch027
  ReferenceAxis = -> Sketch027 [N_Axis]
  Refine = true
  Suppressed = false
  Type = 0
FEATURE [PartDesign::Thickness] Thickness001
  Base = -> Pad014 [Face9]
  BaseFeature = -> Pad014
  Intersection = false
  Join = 0
  Mode = 0
  Refine = true
  Reversed = true
  SupportTransform = false
  Suppressed = false
  Value = 2
FEATURE [PartDesign::SubShapeBinder] Binder001
  BindCopyOnChange = 0
  BindMode = 0
  ClaimChildren = false
  Context = -> Board_58ce [Part001.Body011.Binder001.]
  Fuse = false
  MakeFace = true
  OffsetFill = false
  OffsetIntersection = false
  OffsetJoinType = 0
  OffsetOpenResult = false
  PartialLoad = false
  Refine = true
  Relative = true
  Support = -> [Step_Models_58ce[Top_58ce.S6_SKRHADE_66ce9957abdd_ln_.Part__Feature.Edge656,Top_58ce.S6_SKRHADE_66ce9957abdd_ln_.Part__Feature.Edge660,Top_58ce.SKRHADE.Part__Feature.Edge656,Top_58ce.SKRHADE.Part__Feature.Edge660]]
  _Version = 2
FEATURE [Sketcher::SketchObject] Sketch029
  ArcFitTolerance = 1e-06
  AttachmentSupport = -> [Thickness001]
  ExternalGeometry = -> [Binder001]
  FullyConstrained = false
  MakeInternals = false
  MapMode = 5
  Placement = pos=(0,0,5) rot=(0,0,1;0rad)
  sketch-geometry (6):
    g0: LineSegment [constr] StartX=11.8395 StartY=28.5203 StartZ=0 EndX=10.4199 EndY=28.5203 EndZ=0
    g1: LineSegment [constr] StartX=10.9645 StartY=27.6453 StartZ=0 EndX=10.9645 EndY=28.5203 EndZ=0
    g2: LineSegment [constr] StartX=11.8395 StartY=9.96447 StartZ=0 EndX=10.2544 EndY=9.96447 EndZ=0
    g3: LineSegment [constr] StartX=10.9645 StartY=9.08947 StartZ=0 EndX=10.9645 EndY=9.96447 EndZ=0
    g4: Circle CenterX=10.9645 CenterY=9.96447 CenterZ=0 NormalX=0 NormalY=0 NormalZ=1 AngleXU=0 Radius=4.5
    g5: Circle CenterX=10.9645 CenterY=28.5203 CenterZ=0 NormalX=0 NormalY=0 NormalZ=1 AngleXU=0 Radius=4.5
  constraints (14):
    c: Symmetric(g-4,g-4,g0)
    c: Horizontal(g0)
    c: Symmetric(g-3,g-3,g1)
    c: PointOnObject(g1,g0)
    c: Vertical(g1)
    c: Symmetric(g-6,g-6,g2)
    c: Horizontal(g2)
    c: Symmetric(g-5,g-5,g3)
    c: PointOnObject(g3,g2)
    c: Vertical(g3)
    c: Diameter(g4) = 9
    c: Coincident(g4,g3)
    c: Diameter(g5) = 9
    c: Coincident(g5,g1)
FEATURE [PartDesign::Pocket] Pocket011
  BaseFeature = -> Thickness001
  Direction = (0,0,-1)
  Length = 5
  Length2 = 5
  Profile = -> Sketch029
  ReferenceAxis = -> Sketch029 [N_Axis]
  Refine = true
  Suppressed = false
  Type = 1
FEATURE [PartDesign::SubShapeBinder] Binder002
  BindCopyOnChange = 0
  BindMode = 0
  ClaimChildren = false
  Context = -> Board_58ce [Part001.Body011.Binder002.]
  Fuse = false
  MakeFace = true
  OffsetFill = false
  OffsetIntersection = false
  OffsetJoinType = 0
  OffsetOpenResult = false
  PartialLoad = false
  Refine = true
  Relative = true
  Support = -> [Board_Geoms_58ce[Pcb_58ce.Edge35,Pcb_58ce.Edge101,Pcb_58ce.Edge134,Pcb_58ce.Edge71]]
  _Version = 2
FEATURE [Sketcher::SketchObject] Sketch030
  ArcFitTolerance = 1e-06
  AttachmentSupport = -> [Pocket011]
  ExternalGeometry = -> [Binder002]
  FullyConstrained = true
  MakeInternals = false
  MapMode = 5
  Placement = pos=(0,0,0) rot=(1,0,0;3.14159rad)
  sketch-geometry (4):
    g0: Circle CenterX=3 CenterY=-3 CenterZ=0 NormalX=0 NormalY=0 NormalZ=1 AngleXU=0 Radius=3
    g1: Circle CenterX=18 CenterY=-3 CenterZ=0 NormalX=0 NormalY=0 NormalZ=1 AngleXU=0 Radius=3
    g2: Circle CenterX=18 CenterY=-42 CenterZ=0 NormalX=0 NormalY=0 NormalZ=1 AngleXU=0 Radius=3
    g3: Circle CenterX=3 CenterY=-42 CenterZ=0 NormalX=0 NormalY=0 NormalZ=1 AngleXU=0 Radius=3
  constraints (8):
    c: Diameter(g0) = 6
    c: Coincident(g0,g-3)
    c: Diameter(g1) = 6
    c: Coincident(g1,g-4)
    c: Diameter(g2) = 6
    c: Coincident(g2,g-5)
    c: Diameter(g3) = 6
    c: Coincident(g3,g-6)
FEATURE [PartDesign::Pad] Pad015
  BaseFeature = -> Pocket011
  Direction = (0,0,-1)
  Length = 10
  Length2 = 10
  Profile = -> Sketch030
  ReferenceAxis = -> Sketch030 [N_Axis]
  Refine = true
  Suppressed = false
  Type = 3
  UpToFace = -> Pocket011 [Face21]
FEATURE [Sketcher::SketchObject] Sketch031
  ArcFitTolerance = 1e-06
  AttachmentSupport = -> [Pad015]
  ExternalGeometry = -> [Pad015]
  FullyConstrained = true
  MakeInternals = false
  MapMode = 5
  Placement = pos=(0,0,0) rot=(1,0,0;3.14159rad)
  sketch-geometry (4):
    g0: Circle CenterX=3 CenterY=-3 CenterZ=0 NormalX=0 NormalY=0 NormalZ=1 AngleXU=0 Radius=1.65
    g1: Circle CenterX=18 CenterY=-3 CenterZ=0 NormalX=0 NormalY=0 NormalZ=1 AngleXU=0 Radius=1.65
    g2: Circle CenterX=18 CenterY=-42 CenterZ=0 NormalX=0 NormalY=0 NormalZ=1 AngleXU=0 Radius=1.65
    g3: Circle CenterX=3 CenterY=-42 CenterZ=0 NormalX=0 NormalY=0 NormalZ=1 AngleXU=0 Radius=1.65
  constraints (8):
    c: Diameter(g0) = 3.3
    c: Coincident(g0,g-3)
    c: Diameter(g1) = 3.3
    c: Coincident(g1,g-4)
    c: Diameter(g2) = 3.3
    c: Coincident(g2,g-5)
    c: Diameter(g3) = 3.3
    c: Coincident(g3,g-6)
FEATURE [PartDesign::Pocket] Pocket012
  BaseFeature = -> Pad015
  Direction = (0,0,1)
  Length = 3.3
  Length2 = 5
  Profile = -> Sketch031
  ReferenceAxis = -> Sketch031 [N_Axis]
  Refine = true
  Suppressed = false
  Type = 0
FEATURE [Sketcher::SketchObject] Sketch032
  ArcFitTolerance = 1e-06
  FullyConstrained = false
  MakeInternals = false
  Placement = pos=(0,0,0) rot=(0,0,1;3.14159rad)
  sketch-geometry (8):
    g0: LineSegment StartX=-23.4 StartY=-44 StartZ=0 EndX=-23.4 EndY=-0.999999 EndZ=0
    g1: ArcOfCircle CenterX=-20 CenterY=-0.999999 CenterZ=0 NormalX=0 NormalY=0 NormalZ=1 AngleXU=-3.14159 Radius=3.4 StartAngle=4.71239 EndAngle=6.28318
    g2: LineSegment StartX=-20 StartY=2.4 StartZ=0 EndX=-0.999999 EndY=2.4 EndZ=0
    g3: ArcOfCircle CenterX=-0.999999 CenterY=-0.999999 CenterZ=0 NormalX=0 NormalY=0 NormalZ=1 AngleXU=1.5708 Radius=3.4 StartAngle=4.71239 EndAngle=6.28318
    g4: LineSegment StartX=2.4 StartY=-0.999999 StartZ=0 EndX=2.4 EndY=-44 EndZ=0
    g5: ArcOfCircle CenterX=-0.999999 CenterY=-44 CenterZ=0 NormalX=0 NormalY=0 NormalZ=1 AngleXU=7.47076e-07 Radius=3.4 StartAngle=4.71239 EndAngle=6.28318
    g6: LineSegment StartX=-0.999999 StartY=-47.4 StartZ=0 EndX=-20 EndY=-47.4 EndZ=0
    g7: ArcOfCircle CenterX=-20 CenterY=-44 CenterZ=0 NormalX=0 NormalY=0 NormalZ=1 AngleXU=-1.5708 Radius=3.4 StartAngle=4.71239 EndAngle=6.28318
  constraints (12):
    c: Vertical(g0)
    c: Coincident(g0,g1)
    c: Coincident(g1,g2)
    c: Horizontal(g2)
    c: Coincident(g2,g3)
    c: Coincident(g3,g4)
    c: Vertical(g4)
    c: Coincident(g4,g5)
    c: Coincident(g5,g6)
    c: Horizontal(g6)
    c: Coincident(g6,g7)
    c: Coincident(g7,g0)
FEATURE [Sketcher::SketchObject] Sketch033
  ArcFitTolerance = 1e-06
  AttachmentSupport = -> [Pocket012]
  ExternalGeometry = -> [Pocket012]
  FullyConstrained = false
  MakeInternals = false
  MapMode = 5
  Placement = pos=(0,47.4,0) rot=(0,0.707107,0.707107;3.14159rad)
  sketch-geometry (8):
    g0: LineSegment StartX=-14.6619 StartY=0 StartZ=0 EndX=-7.26206 EndY=0 EndZ=0
    g1: LineSegment StartX=-7.26206 StartY=0 StartZ=0 EndX=-7.26206 EndY=1.78706 EndZ=0
    g2: LineSegment StartX=-7.55642 StartY=2.08141 StartZ=0 EndX=-14.3676 EndY=2.08141 EndZ=0
    g3: LineSegment StartX=-14.6619 StartY=1.78706 StartZ=0 EndX=-14.6619 EndY=0 EndZ=0
    g4: ArcOfCircle CenterX=-14.3676 CenterY=1.78706 CenterZ=0 NormalX=0 NormalY=0 NormalZ=1 AngleXU=0 Radius=0.294356 StartAngle=1.5708 EndAngle=3.14159
    g5: GeomPoint [constr] X=-14.6619 Y=2.08141 Z=0
    g6: ArcOfCircle CenterX=-7.55642 CenterY=1.78706 CenterZ=0 NormalX=0 NormalY=0 NormalZ=1 AngleXU=0 Radius=0.294356 StartAngle=0 EndAngle=1.5708
    g7: GeomPoint [constr] X=-7.26206 Y=2.08141 Z=0
  constraints (15):
    c: Coincident(g0,g1)
    c: Coincident(g3,g0)
    c: Horizontal(g0)
    c: Horizontal(g2)
    c: Vertical(g1)
    c: Vertical(g3)
    c: PointOnObject(g0,g-3)
    c: PointOnObject(g5,g2)
    c: PointOnObject(g5,g3)
    c: Tangent(g2,g4) = -1.5708
    c: Tangent(g3,g4) = -1.5708
    c: PointOnObject(g7,g1)
    c: PointOnObject(g7,g2)
    c: Tangent(g1,g6) = -1.5708
    c: Tangent(g2,g6) = -1.5708
FEATURE [PartDesign::Pocket] Pocket
  BaseFeature = -> Pocket012
  Direction = (0,-1,2e-16)
  Length = 2
  Length2 = 5
  Profile = -> Sketch033
  ReferenceAxis = -> Sketch033 [N_Axis]
  Refine = true
  Suppressed = false
  Type = 0
FEATURE [PartDesign::Chamfer] Chamfer
  Angle = 45
  Base = -> Pocket [Edge34,Edge33]
  BaseFeature = -> Pocket
  ChamferType = 0
  FlipDirection = false
  Refine = true
  Size = 1
  Size2 = 1
  SupportTransform = false
  Suppressed = false
  UseAllEdges = false
FEATURE [PartDesign::Chamfer] Chamfer002
  Angle = 45
  Base = -> Chamfer [Edge5]
  BaseFeature = -> Chamfer
  ChamferType = 0
  FlipDirection = false
  Refine = true
  Size = 1.5
  Size2 = 1
  SupportTransform = false
  Suppressed = false
  UseAllEdges = false
FEATURE [PartDesign::Body] Body011  label="top"
  AllowCompound = false
  Group = -> [Sketch027,Pad014,Thickness001,Binder001,Sketch029,Pocket011,Binder002,Sketch030,Pad015,Sketch031,Pocket012,Sketch033,Pocket,Chamfer,Chamfer002]
  Origin = -> Origin023
  Tip = -> Chamfer002
FEATURE [App::Part] Part001  label="case"
  Group = -> [Body010,Body011]
  Origin = -> Origin021
FEATURE [App::Part] Board_58ce  label="thumb-cluster"
  Group = -> [Local_CS_58ce,Board_Geoms_58ce,Step_Models_58ce,Part001]
  Origin = -> Origin001
---- part thumbstick-breakout.FCStd = doc fcstd_39c8789a8ab7 ----
FCSTD DOCUMENT  (FreeCAD 1.0RUnknown)
Label: thumbstick-breakout
License: All rights reserved
LicenseURL: https://en.wikipedia.org/wiki/All_rights_reserved
objects: Sketcher::SketchObject×14, App::Part×6, PartDesign::Pad×6, PartDesign::ShapeBinder×5, PartDesign::Pocket×5, PartDesign::Body×4, Part::Feature×3, PartDesign::Thickness×2, PartDesign::CoordinateSystem×1, Part::Ellipsoid×1, PartDesign::Plane×1, PartDesign::Chamfer×1, PartDesign::Revolution×1
note: 88 computed .brp shape members not serialized (recipe doc carries the construction recipe); baked Part::Feature solids carry a one-line shape summary decoded from their .brp

FEATURE [PartDesign::CoordinateSystem] Local_CS_bbd4
  AttacherType = Attacher::AttachEngine3D
  MapMode = 2
FEATURE [Part::Feature] Pcb_bbd4
  Placement = pos=(-137.3,117.78,0) rot=(0,0,1;0rad)
  shape: bbox 25.4 x 31.75 x 1.6 mm, 24 faces (baked)
FEATURE [Sketcher::SketchObject] PCB_Sketch_bbd4
  ArcFitTolerance = 1e-06
  FullyConstrained = false
  MakeInternals = false
  sketch-geometry (4):
    g0: LineSegment StartX=0 StartY=31.75 StartZ=0 EndX=0 EndY=0 EndZ=0
    g1: LineSegment StartX=25.4 StartY=31.75 StartZ=0 EndX=0 EndY=31.75 EndZ=0
    g2: LineSegment StartX=0 StartY=0 StartZ=0 EndX=25.4 EndY=0 EndZ=0
    g3: LineSegment StartX=25.4 StartY=0 StartZ=0 EndX=25.4 EndY=31.75 EndZ=0
  constraints (4):
    c: Coincident(g0,g2)
    c: Coincident(g0,g1)
    c: Coincident(g2,g3)
    c: Coincident(g1,g3)
FEATURE [App::Part] Board_Geoms_bbd4
  Group = -> [Pcb_bbd4,PCB_Sketch_bbd4]
  Origin = -> Origin
FEATURE [Part::Feature] Shape  label="J1_SOLID_4955641dfa02"
  Placement = pos=(12.66,29.4,0) rot=(0,0.707107,0.707107;3.14159rad)
  shape: bbox 4.001 x 3.601 x 0.9007 mm, 670 faces (baked)
FEATURE [App::Part] Top_bbd4
  Group = -> [Shape]
  Origin = -> Origin003
FEATURE [App::Part] Step_Models_bbd4
  Group = -> [Top_bbd4]
  Origin = -> Origin002
FEATURE [App::Part] Board_bbd4  label="thumbstick-breakout"
  Group = -> [Local_CS_bbd4,Board_Geoms_bbd4,Step_Models_bbd4]
  Origin = -> Origin001
FEATURE [Sketcher::SketchObject] Sketch009  label="2.005"
  ArcFitTolerance = 1e-06
  FullyConstrained = false
  MakeInternals = false
  sketch-geometry (8):
    g0: LineSegment StartX=-2.4 StartY=31.75 StartZ=0 EndX=-2.4 EndY=0 EndZ=0
    g1: ArcOfCircle CenterX=4.026e-13 CenterY=0 CenterZ=0 NormalX=0 NormalY=0 NormalZ=1 AngleXU=0 Radius=2.4 StartAngle=3.14159 EndAngle=4.71239
    g2: LineSegment StartX=4.70767e-08 StartY=-2.4 StartZ=0 EndX=25.4 EndY=-2.4 EndZ=0
    g3: ArcOfCircle CenterX=25.4 CenterY=0 CenterZ=0 NormalX=0 NormalY=0 NormalZ=1 AngleXU=0 Radius=2.4 StartAngle=4.71239 EndAngle=6.28318
    g4: LineSegment StartX=27.8 StartY=-7.37231e-07 StartZ=0 EndX=27.8 EndY=31.75 EndZ=0
    g5: ArcOfCircle CenterX=25.4 CenterY=31.75 CenterZ=0 NormalX=0 NormalY=0 NormalZ=1 AngleXU=0 Radius=2.4 StartAngle=0 EndAngle=1.5708
    g6: LineSegment StartX=25.4 StartY=34.15 StartZ=0 EndX=7.84308e-07 EndY=34.15 EndZ=0
    g7: ArcOfCircle CenterX=0 CenterY=31.75 CenterZ=0 NormalX=0 NormalY=0 NormalZ=1 AngleXU=0 Radius=2.4 StartAngle=1.5708 EndAngle=3.14159
  constraints (12):
    c: Vertical(g0)
    c: Coincident(g0,g1)
    c: Coincident(g1,g2)
    c: Horizontal(g2)
    c: Coincident(g2,g3)
    c: Coincident(g3,g4)
    c: Vertical(g4)
    c: Coincident(g4,g5)
    c: Coincident(g5,g6)
    c: Horizontal(g6)
    c: Coincident(g6,g7)
    c: Coincident(g7,g0)
FEATURE [PartDesign::Pad] Pad
  Direction = (0,0,1)
  Length = 3.2
  Length2 = 10
  Profile = -> Sketch009
  ReferenceAxis = -> Sketch009 [N_Axis]
  Refine = true
  Suppressed = false
  Type = 0
FEATURE [PartDesign::Thickness] Thickness001
  Base = -> Pad [Face10]
  BaseFeature = -> Pad
  Intersection = false
  Join = 0
  Mode = 0
  Refine = true
  Reversed = true
  SupportTransform = false
  Suppressed = false
  Value = 2
FEATURE [PartDesign::ShapeBinder] ShapeBinder
  Support = -> [Pcb_bbd4]
  TraceSupport = false
FEATURE [Sketcher::SketchObject] Sketch010
  ArcFitTolerance = 1e-06
  AttachmentSupport = -> [Thickness001]
  ExternalGeometry = -> [ShapeBinder]
  FullyConstrained = true
  MakeInternals = false
  MapMode = 5
  Placement = pos=(0,0,2) rot=(0,0,1;0rad)
  sketch-geometry (4):
    g0: Circle CenterX=2.54 CenterY=29.21 CenterZ=0 NormalX=0 NormalY=0 NormalZ=1 AngleXU=0 Radius=1.25
    g1: Circle CenterX=22.86 CenterY=29.21 CenterZ=0 NormalX=0 NormalY=0 NormalZ=1 AngleXU=0 Radius=1.25
    g2: Circle CenterX=22.86 CenterY=2.54 CenterZ=0 NormalX=0 NormalY=0 NormalZ=1 AngleXU=0 Radius=1.25
    g3: Circle CenterX=2.54 CenterY=2.54 CenterZ=0 NormalX=0 NormalY=0 NormalZ=1 AngleXU=0 Radius=1.25
  constraints (8):
    c: Diameter(g0) = 2.5
    c: Coincident(g0,g-3)
    c: Diameter(g1) = 2.5
    c: Coincident(g1,g-4)
    c: Diameter(g2) = 2.5
    c: Coincident(g2,g-5)
    c: Diameter(g3) = 2.5
    c: Coincident(g3,g-6)
FEATURE [PartDesign::Pocket] Pocket002
  BaseFeature = -> Thickness001
  Direction = (0,0,-1)
  Length = 5
  Length2 = 5
  Profile = -> Sketch010
  ReferenceAxis = -> Sketch010 [N_Axis]
  Refine = true
  Suppressed = false
  Type = 1
FEATURE [PartDesign::ShapeBinder] ShapeBinder003
  Support = -> [Pcb_bbd4]
  TraceSupport = false
FEATURE [Sketcher::SketchObject] Sketch011
  ArcFitTolerance = 1e-06
  AttachmentSupport = -> [Pocket002]
  ExternalGeometry = -> [ShapeBinder003]
  FullyConstrained = true
  MakeInternals = false
  MapMode = 5
  Placement = pos=(0,0,2) rot=(0,0,1;0rad)
  sketch-geometry (14):
    g0: Circle CenterX=9.45 CenterY=24.043 CenterZ=0 NormalX=0 NormalY=0 NormalZ=1 AngleXU=0 Radius=1.5
    g1: Circle CenterX=15.95 CenterY=24.043 CenterZ=0 NormalX=0 NormalY=0 NormalZ=1 AngleXU=0 Radius=1.5
    g2: Circle CenterX=15.95 CenterY=19.543 CenterZ=0 NormalX=0 NormalY=0 NormalZ=1 AngleXU=0 Radius=1.5
    g3: Circle CenterX=19.025 CenterY=18.793 CenterZ=0 NormalX=0 NormalY=0 NormalZ=1 AngleXU=0 Radius=1.5
    g4: Circle CenterX=19.025 CenterY=8.793 CenterZ=0 NormalX=0 NormalY=0 NormalZ=1 AngleXU=0 Radius=1.5
    g5: Circle CenterX=9.45 CenterY=19.543 CenterZ=0 NormalX=0 NormalY=0 NormalZ=1 AngleXU=0 Radius=1.5
    g6: Circle CenterX=6.375 CenterY=18.793 CenterZ=0 NormalX=0 NormalY=0 NormalZ=1 AngleXU=0 Radius=1.5
    g7: Circle CenterX=6.375 CenterY=8.793 CenterZ=0 NormalX=0 NormalY=0 NormalZ=1 AngleXU=0 Radius=1.5
    g8: Circle CenterX=3.97 CenterY=16.293 CenterZ=0 NormalX=0 NormalY=0 NormalZ=1 AngleXU=0 Radius=1.2
    g9: Circle CenterX=3.97 CenterY=13.793 CenterZ=0 NormalX=0 NormalY=0 NormalZ=1 AngleXU=0 Radius=1.2
    g10: Circle CenterX=3.97 CenterY=11.293 CenterZ=0 NormalX=0 NormalY=0 NormalZ=1 AngleXU=0 Radius=1.2
    g11: Circle CenterX=10.2 CenterY=5.063 CenterZ=0 NormalX=0 NormalY=0 NormalZ=1 AngleXU=0 Radius=1.2
    g12: Circle CenterX=12.7 CenterY=5.063 CenterZ=0 NormalX=0 NormalY=0 NormalZ=1 AngleXU=0 Radius=1.2
    g13: Circle CenterX=15.2 CenterY=5.063 CenterZ=0 NormalX=0 NormalY=0 NormalZ=1 AngleXU=0 Radius=1.2
  constraints (28):
    c: Diameter(g0) = 3
    c: Coincident(g0,g-3)
    c: Diameter(g1) = 3
    c: Coincident(g1,g-5)
    c: Diameter(g2) = 3
    c: Coincident(g2,g-6)
    c: Diameter(g3) = 3
    c: Coincident(g3,g-12)
    c: Diameter(g4) = 3
    c: Coincident(g4,g-13)
    c: Diameter(g5) = 3
    c: Coincident(g5,g-4)
    c: Diameter(g6) = 3
    c: Coincident(g6,g-7)
    c: Diameter(g7) = 3
    c: Coincident(g7,g-11)
    c: Diameter(g8) = 2.4
    c: Coincident(g8,g-8)
    c: Diameter(g9) = 2.4
    c: Coincident(g9,g-9)
    c: Diameter(g10) = 2.4
    c: Coincident(g10,g-10)
    c: Diameter(g11) = 2.4
    c: Coincident(g11,g-16)
    c: Diameter(g12) = 2.4
    c: Coincident(g12,g-15)
    c: Diameter(g13) = 2.4
    c: Coincident(g13,g-14)
FEATURE [PartDesign::Pocket] Pocket003
  BaseFeature = -> Pocket002
  Direction = (0,0,-1)
  Length = 1
  Length2 = 5
  Profile = -> Sketch011
  ReferenceAxis = -> Sketch011 [N_Axis]
  Refine = true
  Suppressed = false
  Type = 0
FEATURE [PartDesign::Body] Body  label="base"
  AllowCompound = false
  Group = -> [Sketch009,Pad,Thickness001,ShapeBinder,Sketch010,Pocket002,ShapeBinder003,Sketch011,Pocket003]
  Origin = -> Origin010
  Placement = pos=(0,0,-3.6) rot=(0,0,1;0rad)
  Tip = -> Pocket003
FEATURE [PartDesign::ShapeBinder] ShapeBinder004
  Placement = pos=(-137.3,117.78,0) rot=(0,0,1;0rad)
  Support = -> [Pcb_bbd4]
  TraceSupport = false
FEATURE [Sketcher::SketchObject] Sketch012
  ArcFitTolerance = 1e-06
  AttachmentSupport = -> [ShapeBinder004]
  ExternalGeometry = -> [ShapeBinder004]
  FullyConstrained = false
  MakeInternals = false
  MapMode = 5
  Placement = pos=(-137.3,117.78,0) rot=(0,0,1;0rad)
  sketch-geometry (15):
    g0: Circle CenterX=146.75 CenterY=-93.737 CenterZ=0 NormalX=0 NormalY=0 NormalZ=1 AngleXU=0 Radius=0.2
    g1: Circle CenterX=153.25 CenterY=-93.737 CenterZ=0 NormalX=0 NormalY=0 NormalZ=1 AngleXU=0 Radius=0.2
    g2: Circle CenterX=153.25 CenterY=-98.237 CenterZ=0 NormalX=0 NormalY=0 NormalZ=1 AngleXU=0 Radius=0.2
    g3: Circle CenterX=156.325 CenterY=-98.987 CenterZ=0 NormalX=0 NormalY=0 NormalZ=1 AngleXU=0 Radius=0.2
    g4: Circle CenterX=146.75 CenterY=-98.237 CenterZ=0 NormalX=0 NormalY=0 NormalZ=1 AngleXU=0 Radius=0.2
    g5: Circle CenterX=143.675 CenterY=-98.987 CenterZ=0 NormalX=0 NormalY=0 NormalZ=1 AngleXU=0 Radius=0.2
    g6: Circle CenterX=141.27 CenterY=-101.487 CenterZ=0 NormalX=0 NormalY=0 NormalZ=1 AngleXU=0 Radius=0.2
    g7: Circle CenterX=141.27 CenterY=-103.987 CenterZ=0 NormalX=0 NormalY=0 NormalZ=1 AngleXU=0 Radius=0.2
    g8: Circle CenterX=141.27 CenterY=-106.487 CenterZ=0 NormalX=0 NormalY=0 NormalZ=1 AngleXU=0 Radius=0.2
    g9: Circle CenterX=143.675 CenterY=-108.987 CenterZ=0 NormalX=0 NormalY=0 NormalZ=1 AngleXU=0 Radius=0.2
    g10: Circle CenterX=147.5 CenterY=-112.717 CenterZ=0 NormalX=0 NormalY=0 NormalZ=1 AngleXU=0 Radius=0.2
    g11: Circle CenterX=150 CenterY=-112.717 CenterZ=0 NormalX=0 NormalY=0 NormalZ=1 AngleXU=0 Radius=0.2
    g12: Circle CenterX=152.5 CenterY=-112.717 CenterZ=0 NormalX=0 NormalY=0 NormalZ=1 AngleXU=0 Radius=0.2
    g13: Circle CenterX=152.599 CenterY=-112.925 CenterZ=0 NormalX=0 NormalY=0 NormalZ=1 AngleXU=0 Radius=0.2
    g14: Circle CenterX=156.325 CenterY=-108.987 CenterZ=0 NormalX=0 NormalY=0 NormalZ=1 AngleXU=0 Radius=0.2
  constraints (15):
    c: Coincident(g0,g-3)
    c: Coincident(g1,g-4)
    c: Coincident(g2,g-5)
    c: Coincident(g3,g-6)
    c: Coincident(g4,g-7)
    c: Coincident(g5,g-8)
    c: Coincident(g6,g-9)
    c: Coincident(g7,g-10)
    c: Coincident(g8,g-11)
    c: Coincident(g9,g-12)
    c: Coincident(g10,g-13)
    c: Coincident(g11,g-14)
    c: Coincident(g14,g-16)
    c: Equal(g0, g1-g14) x14
    c: Radius(g0) = 0.2
FEATURE [Sketcher::SketchObject] Sketch013
  ArcFitTolerance = 1e-06
  AttachmentSupport = -> [XY_Plane012]
  ExternalGeometry = -> [ShapeBinder004]
  FullyConstrained = false
  MakeInternals = false
  MapMode = 5
  sketch-geometry (14):
    g0: LineSegment StartX=17.3886 StartY=25.1014 StartZ=0 EndX=8.04245 EndY=25.1014 EndZ=0
    g1: LineSegment StartX=6.375 StartY=18.793 StartZ=0 EndX=2.6831 EndY=18.793 EndZ=0
    g2: LineSegment StartX=2.6831 StartY=18.793 StartZ=0 EndX=2.6831 EndY=8.793 EndZ=0
    g3: LineSegment StartX=2.6831 StartY=8.793 StartZ=0 EndX=6.375 EndY=8.793 EndZ=0
    g4: LineSegment StartX=8.26567 StartY=4.26908 StartZ=0 EndX=16.6861 EndY=4.26908 EndZ=0
    g5: LineSegment StartX=16.6861 StartY=4.26908 StartZ=0 EndX=16.6861 EndY=8.793 EndZ=0
    g6: LineSegment StartX=16.6861 StartY=8.793 StartZ=0 EndX=19.025 EndY=8.793 EndZ=0
    g7: LineSegment StartX=19.025 StartY=8.793 StartZ=0 EndX=19.025 EndY=18.793 EndZ=0
    g8: LineSegment StartX=19.025 StartY=18.793 StartZ=0 EndX=17.3886 EndY=18.793 EndZ=0
    g9: LineSegment StartX=17.3886 StartY=18.793 StartZ=0 EndX=17.3886 EndY=25.1014 EndZ=0
    g10: LineSegment StartX=6.375 StartY=18.793 StartZ=0 EndX=8.04245 EndY=18.793 EndZ=0
    g11: LineSegment StartX=8.04245 StartY=18.793 StartZ=0 EndX=8.04245 EndY=25.1014 EndZ=0
    g12: LineSegment StartX=6.375 StartY=8.793 StartZ=0 EndX=8.26567 EndY=8.793 EndZ=0
    g13: LineSegment StartX=8.26567 StartY=8.793 StartZ=0 EndX=8.26567 EndY=4.26908 EndZ=0
  constraints (30):
    c: Horizontal(g0)
    c: Horizontal(g1)
    c: Coincident(g1,g2)
    c: Vertical(g2)
    c: Coincident(g2,g3)
    c: Horizontal(g3)
    c: Horizontal(g4)
    c: Coincident(g4,g5)
    c: Vertical(g5)
    c: Coincident(g5,g6)
    c: Horizontal(g6)
    c: Coincident(g6,g7)
    c: Coincident(g7,g8)
    c: Horizontal(g8)
    c: Coincident(g8,g9)
    c: Coincident(g9,g0)
    c: Vertical(g9)
    c: Coincident(g7,g-8)
    c: Coincident(g6,g-9)
    c: Coincident(g3,g-10)
    c: Coincident(g1,g10)
    c: Horizontal(g10)
    c: Coincident(g10,g11)
    c: Coincident(g11,g0)
    c: Vertical(g11)
    c: Coincident(g3,g12)
    c: Horizontal(g12)
    c: Coincident(g12,g13)
    c: Coincident(g13,g4)
    c: Vertical(g13)
FEATURE [PartDesign::Pad] Pad001
  Direction = (0,0,1)
  Length = 9.3
  Length2 = 10
  Profile = -> Sketch013
  ReferenceAxis = -> Sketch013 [N_Axis]
  Refine = true
  Suppressed = false
  Type = 0
FEATURE [PartDesign::Pad] Pad002
  BaseFeature = -> Pad001
  Direction = (0,0,1)
  Length = 2
  Length2 = 10
  Profile = -> Sketch012
  ReferenceAxis = -> Sketch012 [N_Axis]
  Refine = true
  Reversed = true
  Suppressed = false
  Type = 0
FEATURE [PartDesign::Body] Body001  label="Body"
  AllowCompound = false
  Group = -> [ShapeBinder004,Sketch012,Sketch013,Pad001,Pad002]
  Origin = -> Origin012
  Tip = -> Pad002
FEATURE [Sketcher::SketchObject] Sketch014  label="2.4"
  ArcFitTolerance = 1e-06
  FullyConstrained = false
  MakeInternals = false
  sketch-geometry (8):
    g0: LineSegment StartX=-2.4 StartY=31.75 StartZ=0 EndX=-2.4 EndY=0 EndZ=0
    g1: ArcOfCircle CenterX=0 CenterY=0 CenterZ=0 NormalX=0 NormalY=0 NormalZ=1 AngleXU=0 Radius=2.4 StartAngle=3.14159 EndAngle=4.71239
    g2: LineSegment StartX=-4e-16 StartY=-2.4 StartZ=0 EndX=25.4 EndY=-2.4 EndZ=0
    g3: ArcOfCircle CenterX=25.4 CenterY=0 CenterZ=0 NormalX=0 NormalY=0 NormalZ=1 AngleXU=1.5708 Radius=2.4 StartAngle=3.14159 EndAngle=4.71239
    g4: LineSegment StartX=27.8 StartY=-4e-16 StartZ=0 EndX=27.8 EndY=31.75 EndZ=0
    g5: ArcOfCircle CenterX=25.4 CenterY=31.75 CenterZ=0 NormalX=0 NormalY=0 NormalZ=1 AngleXU=-3.14159 Radius=2.4 StartAngle=3.14159 EndAngle=4.71239
    g6: LineSegment StartX=25.4 StartY=34.15 StartZ=0 EndX=0 EndY=34.15 EndZ=0
    g7: ArcOfCircle CenterX=0 CenterY=31.75 CenterZ=0 NormalX=0 NormalY=0 NormalZ=1 AngleXU=-1.5708 Radius=2.4 StartAngle=3.14159 EndAngle=4.71239
  constraints (12):
    c: Vertical(g0)
    c: Coincident(g0,g1)
    c: Coincident(g1,g2)
    c: Horizontal(g2)
    c: Coincident(g2,g3)
    c: Coincident(g3,g4)
    c: Vertical(g4)
    c: Coincident(g4,g5)
    c: Coincident(g5,g6)
    c: Horizontal(g6)
    c: Coincident(g6,g7)
    c: Coincident(g7,g0)
FEATURE [PartDesign::ShapeBinder] ShapeBinder005
  Support = -> [Pcb_bbd4]
  TraceSupport = false
FEATURE [Sketcher::SketchObject] Sketch
  ArcFitTolerance = 1e-06
  AttachmentSupport = -> [XY_Plane013]
  ExternalGeometry = -> [ShapeBinder005]
  FullyConstrained = true
  MakeInternals = false
  MapMode = 5
  sketch-geometry (2):
    g0: LineSegment [constr] StartX=6.375 StartY=18.793 StartZ=0 EndX=19.025 EndY=8.793 EndZ=0
    g1: Circle CenterX=12.7 CenterY=13.793 CenterZ=0 NormalX=0 NormalY=0 NormalZ=1 AngleXU=0 Radius=2
  constraints (4):
    c: Coincident(g0,g-3)
    c: Coincident(g0,g-5)
    c: Symmetric(g0,g0,g1)
    c: Diameter(g1) = 4
FEATURE [PartDesign::Pad] Pad003
  Direction = (0,0,1)
  Length = 12
  Length2 = 10
  Profile = -> Sketch
  ReferenceAxis = -> Sketch [N_Axis]
  Refine = true
  Suppressed = false
  Type = 0
FEATURE [PartDesign::Body] Body002  label="stick"
  AllowCompound = false
  Group = -> [ShapeBinder005,Sketch,Pad003]
  Origin = -> Origin013
  Placement = pos=(0,0,6.5) rot=(0,0,1;0rad)
  Tip = -> Pad003
FEATURE [Part::Feature] Part__Feature001  label="Thumbstick"
  Placement = pos=(12.7,13.8,-2.8) rot=(0,0,1;0rad)
  shape: bbox 24.74 x 24.74 x 17.5 mm, 20 faces (baked)
FEATURE [App::Part] Part  label="thumbstick"
  Group = -> [Body001,Body002,Part__Feature001]
  Origin = -> Origin011
FEATURE [Sketcher::SketchObject] Sketch015  label="2.006"
  ArcFitTolerance = 1e-06
  FullyConstrained = false
  MakeInternals = false
  sketch-geometry (8):
    g0: LineSegment StartX=-2.4 StartY=31.75 StartZ=0 EndX=-2.4 EndY=0 EndZ=0
    g1: ArcOfCircle CenterX=0 CenterY=0 CenterZ=0 NormalX=0 NormalY=0 NormalZ=1 AngleXU=0 Radius=2.4 StartAngle=3.14159 EndAngle=4.71239
    g2: LineSegment StartX=-4e-16 StartY=-2.4 StartZ=0 EndX=25.4 EndY=-2.4 EndZ=0
    g3: ArcOfCircle CenterX=25.4 CenterY=0 CenterZ=0 NormalX=0 NormalY=0 NormalZ=1 AngleXU=1.5708 Radius=2.4 StartAngle=3.14159 EndAngle=4.71239
    g4: LineSegment StartX=27.8 StartY=-7e-16 StartZ=0 EndX=27.8 EndY=31.75 EndZ=0
    g5: ArcOfCircle CenterX=25.4 CenterY=31.75 CenterZ=0 NormalX=0 NormalY=0 NormalZ=1 AngleXU=-3.14159 Radius=2.4 StartAngle=3.14159 EndAngle=4.71239
    g6: LineSegment StartX=25.4 StartY=34.15 StartZ=0 EndX=0 EndY=34.15 EndZ=0
    g7: ArcOfCircle CenterX=0 CenterY=31.75 CenterZ=0 NormalX=0 NormalY=0 NormalZ=1 AngleXU=-1.5708 Radius=2.4 StartAngle=3.14159 EndAngle=4.71239
  constraints (12):
    c: Vertical(g0)
    c: Coincident(g0,g1)
    c: Coincident(g1,g2)
    c: Horizontal(g2)
    c: Coincident(g2,g3)
    c: Coincident(g3,g4)
    c: Vertical(g4)
    c: Coincident(g4,g5)
    c: Coincident(g5,g6)
    c: Horizontal(g6)
    c: Coincident(g6,g7)
    c: Coincident(g7,g0)
FEATURE [PartDesign::Pad] Pad004
  Direction = (0,0,1)
  Length = 5.3
  Length2 = 10
  Profile = -> Sketch015
  ReferenceAxis = -> Sketch015 [N_Axis]
  Refine = true
  Suppressed = false
  Type = 0
FEATURE [PartDesign::Thickness] Thickness
  Base = -> Pad004 [Face9]
  BaseFeature = -> Pad004
  Intersection = false
  Join = 0
  Mode = 0
  Refine = true
  Reversed = true
  SupportTransform = false
  Suppressed = false
  Value = 2
FEATURE [PartDesign::ShapeBinder] ShapeBinder006
  Support = -> [Pocket003]
  TraceSupport = false
FEATURE [Sketcher::SketchObject] Sketch016
  ArcFitTolerance = 1e-06
  AttachmentSupport = -> [Thickness]
  ExternalGeometry = -> [ShapeBinder006]
  FullyConstrained = true
  MakeInternals = false
  MapMode = 5
  Placement = pos=(0,0,0) rot=(1,0,0;3.14159rad)
  sketch-geometry (8):
    g0: Circle CenterX=2.54 CenterY=-2.54 CenterZ=0 NormalX=0 NormalY=0 NormalZ=1 AngleXU=0 Radius=3
    g1: Circle CenterX=22.86 CenterY=-2.54 CenterZ=0 NormalX=0 NormalY=0 NormalZ=1 AngleXU=0 Radius=3
    g2: Circle CenterX=22.86 CenterY=-29.21 CenterZ=0 NormalX=0 NormalY=0 NormalZ=1 AngleXU=0 Radius=3
    g3: Circle CenterX=2.54 CenterY=-29.21 CenterZ=0 NormalX=0 NormalY=0 NormalZ=1 AngleXU=0 Radius=3
    g4: Circle CenterX=2.54 CenterY=-2.54 CenterZ=0 NormalX=0 NormalY=0 NormalZ=1 AngleXU=0 Radius=1.65
    g5: Circle CenterX=22.86 CenterY=-2.54 CenterZ=0 NormalX=0 NormalY=0 NormalZ=1 AngleXU=0 Radius=1.65
    g6: Circle CenterX=22.86 CenterY=-29.21 CenterZ=0 NormalX=0 NormalY=0 NormalZ=1 AngleXU=0 Radius=1.65
    g7: Circle CenterX=2.54 CenterY=-29.21 CenterZ=0 NormalX=0 NormalY=0 NormalZ=1 AngleXU=0 Radius=1.65
  constraints (16):
    c: Diameter(g0) = 6
    c: Coincident(g0,g-3)
    c: Diameter(g1) = 6
    c: Coincident(g1,g-4)
    c: Diameter(g2) = 6
    c: Coincident(g2,g-5)
    c: Diameter(g3) = 6
    c: Coincident(g3,g-6)
    c: Diameter(g4) = 3.3
    c: Coincident(g4,g0)
    c: Diameter(g5) = 3.3
    c: Coincident(g5,g1)
    c: Diameter(g6) = 3.3
    c: Coincident(g6,g2)
    c: Diameter(g7) = 3.3
    c: Coincident(g7,g3)
FEATURE [Part::Ellipsoid] Ellipsoid
  Angle1 = -90
  Angle2 = 90
  Angle3 = 180
  AttacherType = Attacher::AttachEngine3D
  Placement = pos=(12.7,13.8,9.3) rot=(1,0,0;1.5708rad)
  Radius1 = 12.37
  Radius2 = 12.37
  Radius3 = 8
FEATURE [PartDesign::Plane] DatumPlane
  AttachmentOffset = pos=(0,0,12.7) rot=(0,0,1;0rad)
  AttachmentSupport = -> [YZ_Plane014]
  Length = 70.0266
  MapMode = 5
  Placement = pos=(12.7,0,0) rot=(0.57735,0.57735,0.57735;2.0944rad)
  ResizeMode = 0
  Width = 60.8766
FEATURE [Sketcher::SketchObject] Sketch017
  ArcFitTolerance = 1e-06
  AttachmentSupport = -> [DatumPlane]
  FullyConstrained = false
  MakeInternals = false
  MapMode = 5
  Placement = pos=(12.7,0,0) rot=(0.57735,0.57735,0.57735;2.0944rad)
  sketch-geometry (18):
    g0: Circle [constr] CenterX=29.1118 CenterY=3.8 CenterZ=0 NormalX=0 NormalY=0 NormalZ=1 AngleXU=0 Radius=1
    g1: Circle [constr] CenterX=30.0485 CenterY=13.7535 CenterZ=0 NormalX=0 NormalY=0 NormalZ=1 AngleXU=0 Radius=1
    g2: Circle [constr] CenterX=23.3909 CenterY=17.1877 CenterZ=0 NormalX=0 NormalY=0 NormalZ=1 AngleXU=0 Radius=1
    g3: BSplineCurve PolesCount=3 KnotsCount=2 Degree=2 IsPeriodic=0
    g4: GeomPoint [constr] X=29.1118 Y=3.8 Z=0
    g5: GeomPoint [constr] X=23.3909 Y=17.1877 Z=0
    g6: LineSegment StartX=23.3909 StartY=17.1877 StartZ=0 EndX=13.7824 EndY=17.1877 EndZ=0
    g7: Circle [constr] CenterX=28.1118 CenterY=3.8 CenterZ=0 NormalX=0 NormalY=0 NormalZ=1 AngleXU=0 Radius=1
    g8: Circle [constr] CenterX=28.4002 CenterY=12.6207 CenterZ=0 NormalX=0 NormalY=0 NormalZ=1 AngleXU=0 Radius=1
    g9: Circle [constr] CenterX=23.1917 CenterY=16.2077 CenterZ=0 NormalX=0 NormalY=0 NormalZ=1 AngleXU=0 Radius=1
    g10: BSplineCurve PolesCount=3 KnotsCount=2 Degree=2 IsPeriodic=0
    g11: GeomPoint [constr] X=28.1118 Y=3.8 Z=0
    g12: GeomPoint [constr] X=23.1917 Y=16.2077 Z=0
    g13: LineSegment StartX=28.1118 StartY=3.8 StartZ=0 EndX=29.1118 EndY=3.8 EndZ=0
    g14: LineSegment StartX=13.7824 StartY=17.1877 StartZ=0 EndX=13.7824 EndY=16.2077 EndZ=0
    g15: LineSegment StartX=13.7824 StartY=16.2077 StartZ=0 EndX=23.1917 EndY=16.2077 EndZ=0
    g16: LineSegment [constr] StartX=1.40969 StartY=9.23031 StartZ=0 EndX=26.155 EndY=9.23031 EndZ=0
    g17: LineSegment [constr] StartX=13.7824 StartY=9.23031 StartZ=0 EndX=13.7824 EndY=17.9973 EndZ=0
  constraints (33):
    c: Weight(g0) = 1
    c: Equal(g0,g1)
    c: Equal(g0,g2)
    c: InternalAlignment(g0,g3)
    c: InternalAlignment(g1,g3)
    c: InternalAlignment(g2,g3)
    c: InternalAlignment(g4,g3)
    c: InternalAlignment(g5,g3)
    c: Coincident(g6,g3)
    c: Horizontal(g6)
    c: Weight(g7) = 1
    c: Equal(g7,g8)
    c: Equal(g7,g9)
    c: InternalAlignment(g7,g10)
    c: InternalAlignment(g8,g10)
    c: InternalAlignment(g9,g10)
    c: InternalAlignment(g11,g10)
    c: InternalAlignment(g12,g10)
    c: Coincident(g13,g10)
    c: Coincident(g13,g3)
    c: Horizontal(g13)
    c: DistanceX(g13,g13) = 1
    c: Distance(g3,g10) = 1
    c: Distance(g1,g8) = 2
    c: Coincident(g6,g14)
    c: Vertical(g14)
    c: Coincident(g15,g10)
    c: Horizontal(g15)
    c: Horizontal(g16)
    c: Symmetric(g16,g16,g17)
    c: Vertical(g17)
    c: PointOnObject(g6,g17)
    c: Distance(g10,g-3) = 1.5
FEATURE [PartDesign::Chamfer] Chamfer
  Angle = 45
  Base = -> Thickness [Edge4]
  BaseFeature = -> Thickness
  ChamferType = 0
  FlipDirection = false
  Refine = true
  Size = 1.5
  Size2 = 1
  SupportTransform = false
  Suppressed = false
  UseAllEdges = false
FEATURE [PartDesign::Pad] Pad005
  BaseFeature = -> Chamfer
  Direction = (0,0,-1)
  Length = 3.3
  Length2 = 10
  Profile = -> Sketch016
  ReferenceAxis = -> Sketch016 [N_Axis]
  Refine = true
  Reversed = true
  Suppressed = false
  Type = 0
FEATURE [PartDesign::Revolution] Revolution
  Angle = 360
  Angle2 = 60
  Axis = (0,0,-1)
  Base = (12.7,13.7824,17.1877)
  BaseFeature = -> Pad005
  Profile = -> Sketch017
  ReferenceAxis = -> Sketch017 [Edge4]
  Refine = true
  Reversed = true
  Suppressed = false
  Type = 0
FEATURE [Sketcher::SketchObject] Sketch018
  ArcFitTolerance = 1e-06
  AttachmentSupport = -> [Revolution]
  ExternalGeometry = -> [Revolution]
  FullyConstrained = true
  MakeInternals = false
  MapMode = 5
  Placement = pos=(0,0,17.1877) rot=(0,0,1;0rad)
  sketch-geometry (1):
    g0: Circle CenterX=12.7 CenterY=13.7824 CenterZ=0 NormalX=0 NormalY=0 NormalZ=1 AngleXU=0 Radius=9.5
  constraints (2):
    c: Coincident(g0,g-3)
    c: Diameter(g0) = 19
FEATURE [PartDesign::Pocket] Pocket
  BaseFeature = -> Revolution
  Direction = (0,0,-1)
  Length = 14
  Length2 = 5
  Profile = -> Sketch018
  ReferenceAxis = -> Sketch018 [N_Axis]
  Refine = true
  Suppressed = false
  Type = 0
FEATURE [Sketcher::SketchObject] Sketch019
  ArcFitTolerance = 1e-06
  AttachmentSupport = -> [Pocket]
  FullyConstrained = true
  MakeInternals = false
  MapMode = 5
  Placement = pos=(0,0,5.3) rot=(0,0,1;0rad)
  sketch-geometry (1):
    g0: Circle CenterX=12.7 CenterY=13.7824 CenterZ=0 NormalX=0 NormalY=0 NormalZ=1 AngleXU=0 Radius=14.157
  constraints (2):
    c: Coincident(g0,g-3)
    c: Equal(g0,g-3)
FEATURE [PartDesign::Pocket] Pocket004
  BaseFeature = -> Pocket
  Direction = (0,0,-1)
  Length = 2
  Length2 = 5
  Profile = -> Sketch019
  ReferenceAxis = -> Sketch019 [N_Axis]
  Refine = true
  Suppressed = false
  Type = 0
FEATURE [Sketcher::SketchObject] Sketch020
  ArcFitTolerance = 1e-06
  AttachmentSupport = -> [Pocket004]
  ExternalGeometry = -> [Pocket004]
  FullyConstrained = false
  MakeInternals = false
  MapMode = 5
  Placement = pos=(0,34.15,0) rot=(0,0.707107,0.707107;3.14159rad)
  sketch-geometry (4):
    g0: LineSegment StartX=-15.1629 StartY=0 StartZ=0 EndX=-10.1629 EndY=0 EndZ=0
    g1: LineSegment StartX=-10.1629 StartY=0 StartZ=0 EndX=-10.1629 EndY=1.3 EndZ=0
    g2: LineSegment StartX=-10.1629 StartY=1.3 StartZ=0 EndX=-15.1629 EndY=1.3 EndZ=0
    g3: LineSegment StartX=-15.1629 StartY=1.3 StartZ=0 EndX=-15.1629 EndY=0 EndZ=0
  constraints (11):
    c: Coincident(g0,g1)
    c: Coincident(g1,g2)
    c: Coincident(g2,g3)
    c: Coincident(g3,g0)
    c: Horizontal(g0)
    c: Horizontal(g2)
    c: Vertical(g1)
    c: Vertical(g3)
    c: PointOnObject(g0,g-3)
    c: DistanceX(g2,g2) = 5
    c: DistanceY(g1,g1) = 1.3
FEATURE [PartDesign::Pocket] Pocket005
  BaseFeature = -> Pocket004
  Direction = (0,-1,2e-16)
  Length = 2
  Length2 = 5
  Profile = -> Sketch020
  ReferenceAxis = -> Sketch020 [N_Axis]
  Refine = true
  Suppressed = false
  Type = 0
FEATURE [PartDesign::Body] Body003  label="top"
  AllowCompound = false
  Group = -> [Sketch015,Pad004,Thickness,Chamfer,ShapeBinder006,Sketch016,Pad005,DatumPlane,Sketch017,Revolution,Sketch018,Pocket,Sketch019,Pocket004,Sketch020,Pocket005]
  Origin = -> Origin014
  Tip = -> Pocket005
FEATURE [App::Part] Part001  label="case"
  Group = -> [Body,Body003,Ellipsoid]
  Origin = -> Origin009
